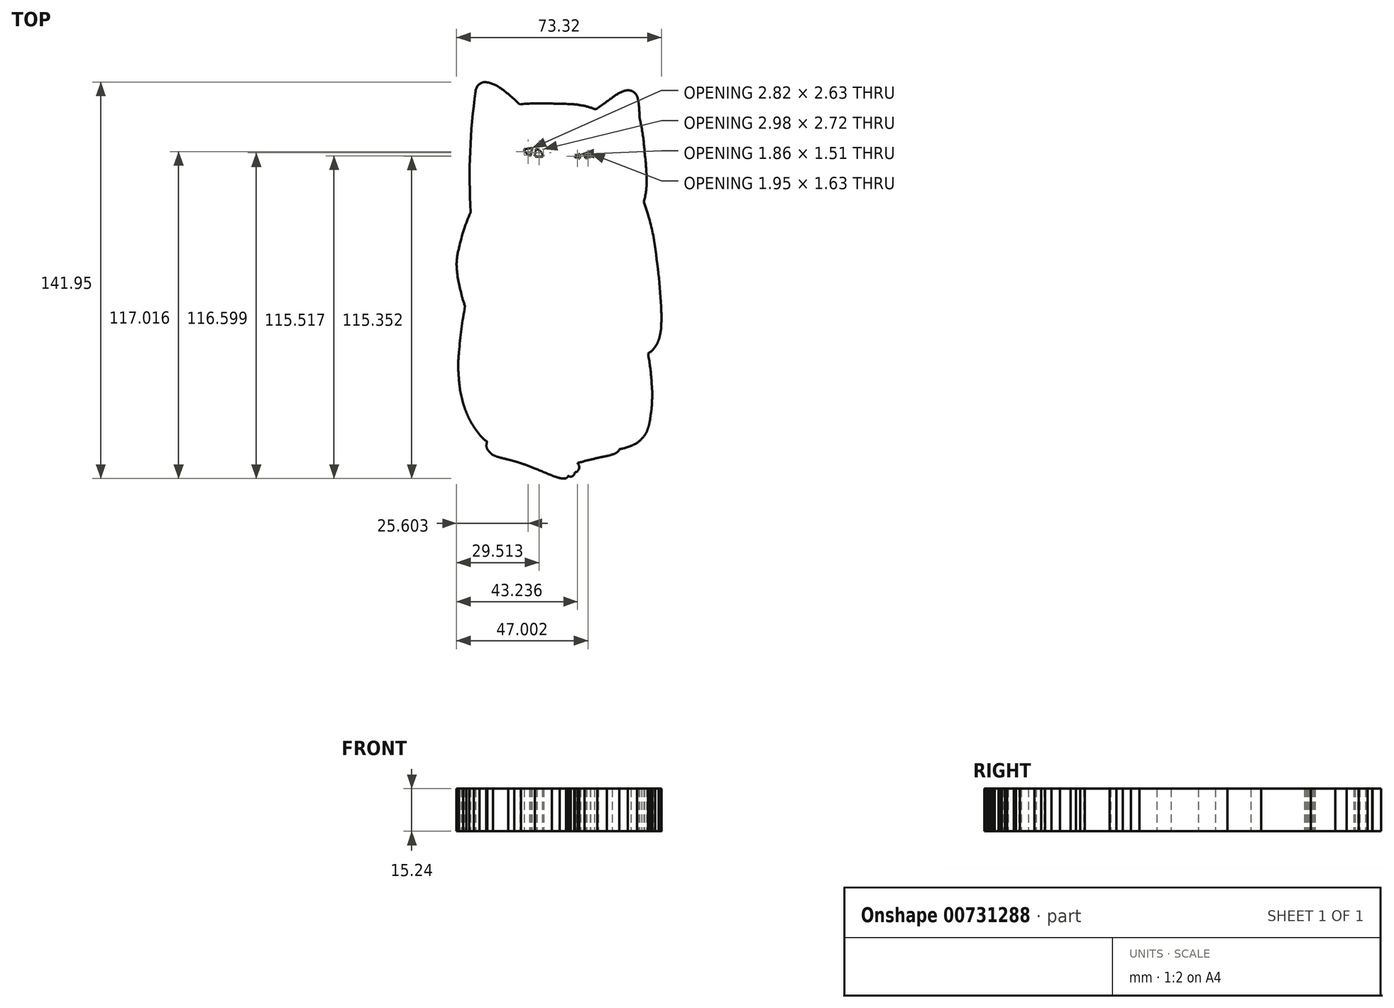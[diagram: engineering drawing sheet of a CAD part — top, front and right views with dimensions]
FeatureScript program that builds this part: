
annotation { "Feature Type Name" : "Feature", "Feature Type Description" : "" }
export const myFeature = defineFeature(function(context is Context, id is Id, definition is map)
    precondition{}
    {
        {
            var Q0;
            Q0=qCreatedBy(makeId("Top.planeOp"),FACE);
            var sketch = newSketch(context, id + "F0", { "sketchPlane" : qUnion([Q0])});
            skArc(sketch, "E0", {"start": v(-13.26, 64.15) * mm, "mid": v(-16.58, 67.18) * mm, "end": v(-20.13, 69.95) * mm});
            skArc(sketch, "E1", {"start": v(-20.13, 69.95) * mm, "mid": v(-22.73, 71.4) * mm, "end": v(-25.6, 72.18) * mm});
            skArc(sketch, "E2", {"start": v(-25.6, 72.18) * mm, "mid": v(-27.98, 71.2) * mm, "end": v(-29.08, 68.87) * mm});
            skArc(sketch, "E3", {"start": v(-29.08, 68.87) * mm, "mid": v(-31.04, 47.27) * mm, "end": v(-30.86, 25.58) * mm});
            skArc(sketch, "E4", {"start": v(-30.86, 25.58) * mm, "mid": v(-33.27, 19.33) * mm, "end": v(-35, 12.84) * mm});
            skArc(sketch, "E5", {"start": v(-35, 12.84) * mm, "mid": v(-35.66, 9.87) * mm, "end": v(-35.9, 6.83) * mm});
            skArc(sketch, "E6", {"start": v(-35.9, 6.83) * mm, "mid": v(-35.42, 1.9) * mm, "end": v(-34.32, -2.92) * mm});
            skArc(sketch, "E7", {"start": v(-34.32, -2.92) * mm, "mid": v(-33.74, -5.52) * mm, "end": v(-32.84, -8.04) * mm});
            skArc(sketch, "E8", {"start": v(-32.84, -8.04) * mm, "mid": v(-34.18, -16.26) * mm, "end": v(-35.03, -24.54) * mm});
            skArc(sketch, "E9", {"start": v(-35.03, -24.54) * mm, "mid": v(-35.3, -29.36) * mm, "end": v(-35.03, -34.17) * mm});
            skArc(sketch, "E10", {"start": v(-35.03, -34.17) * mm, "mid": v(-34.53, -38.6) * mm, "end": v(-33.48, -42.95) * mm});
            skArc(sketch, "E11", {"start": v(-33.48, -42.95) * mm, "mid": v(-33.01, -44.52) * mm, "end": v(-32.42, -46.04) * mm});
            skArc(sketch, "E12", {"start": v(-32.42, -46.04) * mm, "mid": v(-31.91, -47.22) * mm, "end": v(-31.4, -48.4) * mm});
            skArc(sketch, "E13", {"start": v(-31.4, -48.4) * mm, "mid": v(-30.6, -49.87) * mm, "end": v(-29.68, -51.27) * mm});
            skArc(sketch, "E14", {"start": v(-29.68, -51.27) * mm, "mid": v(-28.72, -52.66) * mm, "end": v(-27.72, -54.01) * mm});
            skArc(sketch, "E15", {"start": v(-27.72, -54.01) * mm, "mid": v(-26.47, -55.38) * mm, "end": v(-25.05, -56.58) * mm});
            skLineSegment(sketch, "E16", {"start": v(-24.94, -56.63) * mm, "end": v(-25.05, -56.58) * mm});
            skArc(sketch, "E17", {"start": v(-24.94, -56.63) * mm, "mid": v(-25.12, -57.06) * mm, "end": v(-25.2, -57.51) * mm});
            skArc(sketch, "E18", {"start": v(-25.2, -57.51) * mm, "mid": v(-25.2, -58.34) * mm, "end": v(-24.94, -59.13) * mm});
            skArc(sketch, "E19", {"start": v(-24.94, -59.13) * mm, "mid": v(-24.05, -60.33) * mm, "end": v(-22.9, -61.28) * mm});
            skArc(sketch, "E20", {"start": v(-22.9, -61.28) * mm, "mid": v(-21.83, -61.78) * mm, "end": v(-20.7, -62.14) * mm});
            skArc(sketch, "E21", {"start": v(-20.7, -62.14) * mm, "mid": v(-19.06, -62.56) * mm, "end": v(-17.43, -62.98) * mm});
            skArc(sketch, "E22", {"start": v(-15.23, -63.56) * mm, "mid": v(-16.33, -63.26) * mm, "end": v(-17.43, -62.98) * mm});
            skArc(sketch, "E23", {"start": v(-12.9, -64.3) * mm, "mid": v(-14.05, -63.9) * mm, "end": v(-15.23, -63.56) * mm});
            skArc(sketch, "E24", {"start": v(-7.9, -66.1) * mm, "mid": v(-10.38, -65.15) * mm, "end": v(-12.9, -64.3) * mm});
            skArc(sketch, "E25", {"start": v(-7.9, -66.1) * mm, "mid": v(-4.84, -67.4) * mm, "end": v(-1.78, -68.67) * mm});
            skArc(sketch, "E26", {"start": v(-1.78, -68.67) * mm, "mid": v(-0.43, -69.15) * mm, "end": v(0.95, -69.56) * mm});
            skArc(sketch, "E27", {"start": v(0.95, -69.56) * mm, "mid": v(2.1, -69.76) * mm, "end": v(3.24, -69.7) * mm});
            skArc(sketch, "E28", {"start": v(3.24, -69.7) * mm, "mid": v(3.75, -69.3) * mm, "end": v(4.13, -68.77) * mm});
            skArc(sketch, "E29", {"start": v(4.13, -68.77) * mm, "mid": v(4.48, -69.01) * mm, "end": v(4.9, -69.08) * mm});
            skArc(sketch, "E30", {"start": v(4.9, -69.08) * mm, "mid": v(5.7, -68.84) * mm, "end": v(6.24, -68.22) * mm});
            skArc(sketch, "E31", {"start": v(6.24, -68.22) * mm, "mid": v(6.4, -67.87) * mm, "end": v(6.5, -67.5) * mm});
            skArc(sketch, "E32", {"start": v(6.5, -67.5) * mm, "mid": v(7.09, -67.37) * mm, "end": v(7.53, -66.97) * mm});
            skArc(sketch, "E33", {"start": v(7.53, -66.97) * mm, "mid": v(7.79, -66.56) * mm, "end": v(7.96, -66.1) * mm});
            skArc(sketch, "E34", {"start": v(7.96, -66.1) * mm, "mid": v(7.96, -65.4) * mm, "end": v(7.72, -64.72) * mm});
            skArc(sketch, "E35", {"start": v(7.72, -64.72) * mm, "mid": v(7.62, -64.55) * mm, "end": v(7.46, -64.43) * mm});
            skLineSegment(sketch, "E36", {"start": v(7.46, -64.43) * mm, "end": v(7.46, -64.1) * mm});
            skArc(sketch, "E37", {"start": v(7.46, -64.1) * mm, "mid": v(8.7, -63.87) * mm, "end": v(9.9, -63.5) * mm});
            skArc(sketch, "E38", {"start": v(9.9, -63.5) * mm, "mid": v(12.18, -62.96) * mm, "end": v(14.45, -62.4) * mm});
            skArc(sketch, "E39", {"start": v(17.95, -61.7) * mm, "mid": v(16.2, -62.03) * mm, "end": v(14.45, -62.4) * mm});
            skArc(sketch, "E40", {"start": v(17.95, -61.7) * mm, "mid": v(19.35, -61.32) * mm, "end": v(20.72, -60.84) * mm});
            skArc(sketch, "E41", {"start": v(20.72, -60.84) * mm, "mid": v(21.72, -60.22) * mm, "end": v(22.4, -59.25) * mm});
            skArc(sketch, "E42", {"start": v(22.4, -59.25) * mm, "mid": v(23.94, -58.94) * mm, "end": v(25.44, -58.44) * mm});
            skArc(sketch, "E43", {"start": v(25.44, -58.44) * mm, "mid": v(27.08, -57.83) * mm, "end": v(28.65, -57.04) * mm});
            skArc(sketch, "E44", {"start": v(28.65, -57.04) * mm, "mid": v(30.19, -55.73) * mm, "end": v(31.48, -54.18) * mm});
            skArc(sketch, "E45", {"start": v(31.48, -54.18) * mm, "mid": v(32.14, -53.05) * mm, "end": v(32.57, -51.82) * mm});
            skArc(sketch, "E46", {"start": v(32.57, -51.82) * mm, "mid": v(32.96, -50.65) * mm, "end": v(33.23, -49.44) * mm});
            skArc(sketch, "E47", {"start": v(33.23, -49.44) * mm, "mid": v(33.35, -48.75) * mm, "end": v(33.42, -48.06) * mm});
            skArc(sketch, "E48", {"start": v(33.78, -45.75) * mm, "mid": v(33.6, -46.9) * mm, "end": v(33.42, -48.06) * mm});
            skArc(sketch, "E49", {"start": v(33.78, -45.75) * mm, "mid": v(33.95, -44.24) * mm, "end": v(34, -42.72) * mm});
            skArc(sketch, "E50", {"start": v(34, -42.72) * mm, "mid": v(34.12, -40.83) * mm, "end": v(34.12, -38.94) * mm});
            skArc(sketch, "E51", {"start": v(34.12, -38.94) * mm, "mid": v(34.08, -37.98) * mm, "end": v(34, -37.02) * mm});
            skArc(sketch, "E52", {"start": v(34, -37.02) * mm, "mid": v(33.96, -36.28) * mm, "end": v(33.89, -35.54) * mm});
            skArc(sketch, "E53", {"start": v(33.89, -35.54) * mm, "mid": v(33.87, -34.66) * mm, "end": v(33.79, -33.8) * mm});
            skArc(sketch, "E54", {"start": v(33.79, -33.8) * mm, "mid": v(33.32, -29.37) * mm, "end": v(32.6, -24.98) * mm});
            skArc(sketch, "E55", {"start": v(32.6, -24.98) * mm, "mid": v(34.05, -23.95) * mm, "end": v(35.17, -22.57) * mm});
            skArc(sketch, "E56", {"start": v(35.17, -22.57) * mm, "mid": v(35.9, -21.46) * mm, "end": v(36.4, -20.23) * mm});
            skArc(sketch, "E57", {"start": v(36.4, -20.23) * mm, "mid": v(36.83, -18.77) * mm, "end": v(37.13, -17.27) * mm});
            skArc(sketch, "E58", {"start": v(37.13, -17.27) * mm, "mid": v(37.34, -15.77) * mm, "end": v(37.37, -14.25) * mm});
            skArc(sketch, "E59", {"start": v(37.37, -14.25) * mm, "mid": v(37.43, -12.1) * mm, "end": v(37.37, -9.95) * mm});
            skArc(sketch, "E60", {"start": v(37.37, -9.95) * mm, "mid": v(36.33, 3.68) * mm, "end": v(34.49, 17.22) * mm});
            skArc(sketch, "E61", {"start": v(34.49, 17.22) * mm, "mid": v(33.01, 23.32) * mm, "end": v(31.1, 29.29) * mm});
            skArc(sketch, "E62", {"start": v(31.1, 29.29) * mm, "mid": v(31.89, 32.94) * mm, "end": v(32.15, 36.67) * mm});
            skArc(sketch, "E63", {"start": v(32.15, 36.67) * mm, "mid": v(31.93, 41.9) * mm, "end": v(31.37, 47.1) * mm});
            skArc(sketch, "E64", {"start": v(31.37, 47.1) * mm, "mid": v(30.99, 51.5) * mm, "end": v(30.34, 55.88) * mm});
            skArc(sketch, "E65", {"start": v(29.54, 59.85) * mm, "mid": v(29.9, 57.86) * mm, "end": v(30.34, 55.88) * mm});
            skArc(sketch, "E66", {"start": v(29.54, 59.85) * mm, "mid": v(29.5, 62.04) * mm, "end": v(29.3, 64.22) * mm});
            skArc(sketch, "E67", {"start": v(29.3, 64.22) * mm, "mid": v(29.06, 65.84) * mm, "end": v(28.54, 67.4) * mm});
            skArc(sketch, "E68", {"start": v(28.54, 67.4) * mm, "mid": v(27.73, 68.42) * mm, "end": v(26.58, 69.03) * mm});
            skArc(sketch, "E69", {"start": v(26.58, 69.03) * mm, "mid": v(25.43, 69.2) * mm, "end": v(24.28, 69.03) * mm});
            skArc(sketch, "E70", {"start": v(24.28, 69.03) * mm, "mid": v(21.94, 68.02) * mm, "end": v(19.85, 66.57) * mm});
            skArc(sketch, "E71", {"start": v(19.85, 66.57) * mm, "mid": v(17.33, 64.79) * mm, "end": v(14.82, 62.99) * mm});
            skArc(sketch, "E72", {"start": v(13.48, 62.46) * mm, "mid": v(14.2, 62.58) * mm, "end": v(14.82, 62.99) * mm});
            skArc(sketch, "E73", {"start": v(13.48, 62.46) * mm, "mid": v(11.03, 63.32) * mm, "end": v(8.5, 63.86) * mm});
            skArc(sketch, "E74", {"start": v(8.5, 63.86) * mm, "mid": v(6.85, 64.12) * mm, "end": v(5.19, 64.26) * mm});
            skArc(sketch, "E75", {"start": v(-4.66, 64.5) * mm, "mid": v(-8.96, 64.5) * mm, "end": v(-13.26, 64.15) * mm});
            skArc(sketch, "E76", {"start": v(5.19, 64.26) * mm, "mid": v(0.27, 64.42) * mm, "end": v(-4.66, 64.5) * mm});
            skArc(sketch, "E77", {"start": v(-25.6, 71.22) * mm, "mid": v(-27.28, 70.55) * mm, "end": v(-27.95, 68.87) * mm});
            skArc(sketch, "E78", {"start": v(-19.39, 68.5) * mm, "mid": v(-22.32, 70.26) * mm, "end": v(-25.6, 71.22) * mm});
            skArc(sketch, "E79", {"start": v(-15.35, 64.85) * mm, "mid": v(-17.26, 66.8) * mm, "end": v(-19.39, 68.5) * mm});
            skArc(sketch, "E80", {"start": v(-14.8, 64.3) * mm, "mid": v(-15.03, 64.62) * mm, "end": v(-15.35, 64.85) * mm});
            skArc(sketch, "E81", {"start": v(-15.09, 63.8) * mm, "mid": v(-14.84, 63.99) * mm, "end": v(-14.8, 64.3) * mm});
            skArc(sketch, "E82", {"start": v(-15.09, 63.8) * mm, "mid": v(-15.34, 63.67) * mm, "end": v(-15.46, 63.4) * mm});
            skArc(sketch, "E83", {"start": v(-15.46, 63.4) * mm, "mid": v(-15.36, 63.1) * mm, "end": v(-15.09, 62.91) * mm});
            skArc(sketch, "E84", {"start": v(-9.42, 63.55) * mm, "mid": v(-12.27, 63.36) * mm, "end": v(-15.09, 62.91) * mm});
            skArc(sketch, "E85", {"start": v(-0.75, 63.55) * mm, "mid": v(-5.09, 63.73) * mm, "end": v(-9.42, 63.55) * mm});
            skArc(sketch, "E86", {"start": v(8.17, 63.12) * mm, "mid": v(3.72, 63.52) * mm, "end": v(-0.75, 63.55) * mm});
            skArc(sketch, "E87", {"start": v(11.74, 62.2) * mm, "mid": v(9.97, 62.74) * mm, "end": v(8.17, 63.12) * mm});
            skArc(sketch, "E88", {"start": v(14.35, 61.15) * mm, "mid": v(13.08, 61.76) * mm, "end": v(11.74, 62.2) * mm});
            skArc(sketch, "E89", {"start": v(15.93, 59.97) * mm, "mid": v(15.2, 60.65) * mm, "end": v(14.35, 61.15) * mm});
            skArc(sketch, "E90", {"start": v(15.93, 59.97) * mm, "mid": v(16.46, 59.95) * mm, "end": v(16.61, 60.46) * mm});
            skArc(sketch, "E91", {"start": v(16.61, 60.46) * mm, "mid": v(16.16, 60.97) * mm, "end": v(15.63, 61.4) * mm});
            skArc(sketch, "E92", {"start": v(15.15, 61.93) * mm, "mid": v(15.32, 61.6) * mm, "end": v(15.63, 61.4) * mm});
            skLineSegment(sketch, "E93", {"start": v(18.79, 64.86) * mm, "end": v(15.22, 62.16) * mm});
            skArc(sketch, "E94", {"start": v(15.22, 62.16) * mm, "mid": v(15.15, 62.05) * mm, "end": v(15.15, 61.93) * mm});
            skArc(sketch, "E95", {"start": v(23.23, 67.61) * mm, "mid": v(20.95, 66.34) * mm, "end": v(18.79, 64.86) * mm});
            skArc(sketch, "E96", {"start": v(26.6, 68.34) * mm, "mid": v(24.85, 68.3) * mm, "end": v(23.23, 67.61) * mm});
            skArc(sketch, "E97", {"start": v(27.67, 67.31) * mm, "mid": v(27.23, 67.92) * mm, "end": v(26.6, 68.34) * mm});
            skArc(sketch, "E98", {"start": v(28.3, 65.47) * mm, "mid": v(28.07, 66.42) * mm, "end": v(27.67, 67.31) * mm});
            skArc(sketch, "E99", {"start": v(28.66, 62.26) * mm, "mid": v(28.56, 63.87) * mm, "end": v(28.3, 65.47) * mm});
            skArc(sketch, "E100", {"start": v(28.66, 62.26) * mm, "mid": v(28.76, 60.61) * mm, "end": v(28.92, 58.97) * mm});
            skArc(sketch, "E101", {"start": v(30, 52.86) * mm, "mid": v(29.82, 54.19) * mm, "end": v(29.62, 55.5) * mm});
            skArc(sketch, "E102", {"start": v(29.62, 55.5) * mm, "mid": v(29.33, 57.25) * mm, "end": v(28.92, 58.97) * mm});
            skArc(sketch, "E103", {"start": v(30.43, 49.6) * mm, "mid": v(30.25, 51.24) * mm, "end": v(30, 52.86) * mm});
            skArc(sketch, "E104", {"start": v(30.43, 49.6) * mm, "mid": v(30.54, 47.86) * mm, "end": v(30.68, 46.12) * mm});
            skArc(sketch, "E105", {"start": v(31, 43.26) * mm, "mid": v(30.86, 44.7) * mm, "end": v(30.68, 46.12) * mm});
            skArc(sketch, "E106", {"start": v(31.21, 40.83) * mm, "mid": v(31.12, 42.05) * mm, "end": v(31, 43.26) * mm});
            skArc(sketch, "E107", {"start": v(31.09, 34.8) * mm, "mid": v(31.16, 37.81) * mm, "end": v(31.21, 40.83) * mm});
            skArc(sketch, "E108", {"start": v(30.6, 31.77) * mm, "mid": v(30.92, 33.27) * mm, "end": v(31.09, 34.8) * mm});
            skArc(sketch, "E109", {"start": v(30.6, 31.77) * mm, "mid": v(30.27, 30.7) * mm, "end": v(29.95, 29.64) * mm});
            skArc(sketch, "E110", {"start": v(31.33, 26) * mm, "mid": v(30.69, 27.84) * mm, "end": v(29.95, 29.64) * mm});
            skArc(sketch, "E111", {"start": v(32.34, 22.74) * mm, "mid": v(31.86, 24.38) * mm, "end": v(31.33, 26) * mm});
            skArc(sketch, "E112", {"start": v(33.01, 19.96) * mm, "mid": v(32.72, 21.36) * mm, "end": v(32.34, 22.74) * mm});
            skArc(sketch, "E113", {"start": v(33.51, 17.52) * mm, "mid": v(33.28, 18.74) * mm, "end": v(33.01, 19.96) * mm});
            skArc(sketch, "E114", {"start": v(33.85, 15.67) * mm, "mid": v(33.71, 16.6) * mm, "end": v(33.51, 17.52) * mm});
            skArc(sketch, "E115", {"start": v(34.55, 11.43) * mm, "mid": v(34.24, 13.56) * mm, "end": v(33.85, 15.67) * mm});
            skArc(sketch, "E116", {"start": v(35.5, 4.62) * mm, "mid": v(35.09, 8.04) * mm, "end": v(34.55, 11.43) * mm});
            skArc(sketch, "E117", {"start": v(35.9, 0) * mm, "mid": v(35.76, 2.32) * mm, "end": v(35.5, 4.62) * mm});
            skArc(sketch, "E118", {"start": v(36.3, -5.46) * mm, "mid": v(36.16, -2.72) * mm, "end": v(35.9, 0) * mm});
            skArc(sketch, "E119", {"start": v(36.4, -9.9) * mm, "mid": v(36.4, -7.67) * mm, "end": v(36.3, -5.46) * mm});
            skArc(sketch, "E120", {"start": v(36.52, -13.76) * mm, "mid": v(36.47, -11.83) * mm, "end": v(36.4, -9.9) * mm});
            skArc(sketch, "E121", {"start": v(36.52, -15.6) * mm, "mid": v(36.54, -14.68) * mm, "end": v(36.52, -13.76) * mm});
            skArc(sketch, "E122", {"start": v(35.65, -19.72) * mm, "mid": v(36.23, -17.7) * mm, "end": v(36.52, -15.6) * mm});
            skArc(sketch, "E123", {"start": v(33.92, -22.57) * mm, "mid": v(34.9, -21.2) * mm, "end": v(35.65, -19.72) * mm});
            skArc(sketch, "E124", {"start": v(31.3, -24.18) * mm, "mid": v(32.74, -23.6) * mm, "end": v(33.92, -22.57) * mm});
            skArc(sketch, "E125", {"start": v(29.61, -23.69) * mm, "mid": v(30.41, -24.08) * mm, "end": v(31.3, -24.18) * mm});
            skArc(sketch, "E126", {"start": v(23.95, -19.4) * mm, "mid": v(26.58, -21.8) * mm, "end": v(29.61, -23.69) * mm});
            skArc(sketch, "E127", {"start": v(20.84, -15.32) * mm, "mid": v(22.33, -17.4) * mm, "end": v(23.95, -19.4) * mm});
            skArc(sketch, "E128", {"start": v(20.84, -15.32) * mm, "mid": v(19.8, -13.6) * mm, "end": v(18.76, -11.87) * mm});
            skArc(sketch, "E129", {"start": v(17.46, -8.91) * mm, "mid": v(18.07, -10.4) * mm, "end": v(18.76, -11.87) * mm});
            skArc(sketch, "E130", {"start": v(16.47, -5.65) * mm, "mid": v(16.93, -7.3) * mm, "end": v(17.46, -8.91) * mm});
            skArc(sketch, "E131", {"start": v(16.47, -5.65) * mm, "mid": v(16.21, -4.49) * mm, "end": v(15.72, -3.4) * mm});
            skArc(sketch, "E132", {"start": v(15.72, -3.4) * mm, "mid": v(15.11, -2.27) * mm, "end": v(14.33, -1.24) * mm});
            skArc(sketch, "E133", {"start": v(14.33, -1.24) * mm, "mid": v(13.47, -0.28) * mm, "end": v(12.45, 0.5) * mm});
            skArc(sketch, "E134", {"start": v(11.14, 3.5) * mm, "mid": v(11.66, 1.94) * mm, "end": v(12.45, 0.5) * mm});
            skArc(sketch, "E135", {"start": v(10.86, 5.84) * mm, "mid": v(10.83, 4.64) * mm, "end": v(11.14, 3.5) * mm});
            skArc(sketch, "E136", {"start": v(11.83, 6.04) * mm, "mid": v(11.32, 6.07) * mm, "end": v(10.86, 5.84) * mm});
            skArc(sketch, "E137", {"start": v(11.83, 6.04) * mm, "mid": v(12.23, 5.93) * mm, "end": v(12.63, 6.04) * mm});
            skArc(sketch, "E138", {"start": v(12.63, 6.04) * mm, "mid": v(12.8, 6.3) * mm, "end": v(12.8, 6.62) * mm});
            skArc(sketch, "E139", {"start": v(13.3, 7.62) * mm, "mid": v(12.9, 7.2) * mm, "end": v(12.8, 6.62) * mm});
            skArc(sketch, "E140", {"start": v(13.81, 7.62) * mm, "mid": v(13.56, 7.71) * mm, "end": v(13.3, 7.62) * mm});
            skArc(sketch, "E141", {"start": v(14.18, 7.16) * mm, "mid": v(14.03, 7.41) * mm, "end": v(13.81, 7.62) * mm});
            skArc(sketch, "E142", {"start": v(14.18, 7.16) * mm, "mid": v(14.47, 7.1) * mm, "end": v(14.75, 7.16) * mm});
            skArc(sketch, "E143", {"start": v(14.75, 7.16) * mm, "mid": v(14.87, 7.35) * mm, "end": v(14.92, 7.56) * mm});
            skArc(sketch, "E144", {"start": v(14.92, 7.56) * mm, "mid": v(14.74, 8.04) * mm, "end": v(14.5, 8.5) * mm});
            skArc(sketch, "E145", {"start": v(13.52, 11.92) * mm, "mid": v(13.94, 10.19) * mm, "end": v(14.5, 8.5) * mm});
            skArc(sketch, "E146", {"start": v(13.17, 14.34) * mm, "mid": v(13.3, 13.12) * mm, "end": v(13.52, 11.92) * mm});
            skArc(sketch, "E147", {"start": v(14.59, 14.59) * mm, "mid": v(13.81, 14.87) * mm, "end": v(13.17, 14.34) * mm});
            skArc(sketch, "E148", {"start": v(16.72, 9.6) * mm, "mid": v(15.7, 12.11) * mm, "end": v(14.59, 14.59) * mm});
            skArc(sketch, "E149", {"start": v(16.72, 9.22) * mm, "mid": v(16.72, 9.4) * mm, "end": v(16.72, 9.6) * mm});
            skArc(sketch, "E150", {"start": v(16.72, 9.22) * mm, "mid": v(16.97, 9) * mm, "end": v(17.31, 8.93) * mm});
            skArc(sketch, "E151", {"start": v(19.27, 9.22) * mm, "mid": v(18.26, 9.3) * mm, "end": v(17.31, 8.93) * mm});
            skArc(sketch, "E152", {"start": v(20.5, 7.32) * mm, "mid": v(20.1, 8.41) * mm, "end": v(19.27, 9.22) * mm});
            skArc(sketch, "E153", {"start": v(20.5, 6.44) * mm, "mid": v(20.51, 6.88) * mm, "end": v(20.5, 7.32) * mm});
            skArc(sketch, "E154", {"start": v(20.5, 6.44) * mm, "mid": v(20.96, 6.2) * mm, "end": v(21.42, 6.44) * mm});
            skArc(sketch, "E155", {"start": v(21.42, 6.44) * mm, "mid": v(21.45, 6.91) * mm, "end": v(21.45, 7.39) * mm});
            skArc(sketch, "E156", {"start": v(21.93, 7.7) * mm, "mid": v(21.62, 7.65) * mm, "end": v(21.45, 7.39) * mm});
            skArc(sketch, "E157", {"start": v(23.1, 7.26) * mm, "mid": v(22.57, 7.65) * mm, "end": v(21.93, 7.7) * mm});
            skArc(sketch, "E158", {"start": v(24.39, 4.96) * mm, "mid": v(23.97, 6.24) * mm, "end": v(23.1, 7.26) * mm});
            skArc(sketch, "E159", {"start": v(24.59, 2.74) * mm, "mid": v(24.56, 3.86) * mm, "end": v(24.39, 4.96) * mm});
            skArc(sketch, "E160", {"start": v(24.39, 1.17) * mm, "mid": v(24.57, 1.95) * mm, "end": v(24.59, 2.74) * mm});
            skArc(sketch, "E161", {"start": v(24.39, 1.17) * mm, "mid": v(24.3, 0.85) * mm, "end": v(24.39, 0.53) * mm});
            skArc(sketch, "E162", {"start": v(24.39, 0.53) * mm, "mid": v(24.75, 0.37) * mm, "end": v(25.14, 0.32) * mm});
            skArc(sketch, "E163", {"start": v(25.14, 0.32) * mm, "mid": v(26.14, -1.9) * mm, "end": v(27.2, -4.1) * mm});
            skArc(sketch, "E164", {"start": v(27.2, -4.1) * mm, "mid": v(28.44, -6.92) * mm, "end": v(29.73, -9.72) * mm});
            skArc(sketch, "E165", {"start": v(29.73, -9.72) * mm, "mid": v(29.67, -10.08) * mm, "end": v(29.73, -10.44) * mm});
            skArc(sketch, "E166", {"start": v(29.73, -10.44) * mm, "mid": v(30.22, -10.95) * mm, "end": v(30.85, -10.63) * mm});
            skArc(sketch, "E167", {"start": v(30.85, -10.63) * mm, "mid": v(30.75, -10.05) * mm, "end": v(30.58, -9.5) * mm});
            skArc(sketch, "E168", {"start": v(30.58, -9.5) * mm, "mid": v(28.14, -4.01) * mm, "end": v(25.63, 1.44) * mm});
            skArc(sketch, "E169", {"start": v(25.51, 1.99) * mm, "mid": v(25.53, 1.7) * mm, "end": v(25.63, 1.44) * mm});
            skArc(sketch, "E170", {"start": v(25.51, 1.99) * mm, "mid": v(25.61, 3.02) * mm, "end": v(25.51, 4.06) * mm});
            skArc(sketch, "E171", {"start": v(25.51, 4.06) * mm, "mid": v(25.26, 5.36) * mm, "end": v(24.7, 6.56) * mm});
            skArc(sketch, "E172", {"start": v(24.7, 6.56) * mm, "mid": v(24.16, 7.47) * mm, "end": v(23.36, 8.17) * mm});
            skArc(sketch, "E173", {"start": v(23.36, 8.17) * mm, "mid": v(22.61, 8.5) * mm, "end": v(21.8, 8.57) * mm});
            skLineSegment(sketch, "E174", {"start": v(21.8, 8.57) * mm, "end": v(21.01, 8.57) * mm});
            skArc(sketch, "E175", {"start": v(21.01, 8.57) * mm, "mid": v(20.34, 9.46) * mm, "end": v(19.39, 10.04) * mm});
            skArc(sketch, "E176", {"start": v(19.39, 10.04) * mm, "mid": v(18.64, 10.24) * mm, "end": v(17.86, 10.16) * mm});
            skArc(sketch, "E177", {"start": v(13.32, 15.8) * mm, "mid": v(12.57, 15.28) * mm, "end": v(12.2, 14.46) * mm});
            skArc(sketch, "E178", {"start": v(15.21, 15.52) * mm, "mid": v(14.3, 15.87) * mm, "end": v(13.32, 15.8) * mm});
            skLineSegment(sketch, "E179", {"start": v(17.86, 10.16) * mm, "end": v(15.57, 15.13) * mm});
            skArc(sketch, "E180", {"start": v(15.57, 15.13) * mm, "mid": v(15.42, 15.35) * mm, "end": v(15.21, 15.52) * mm});
            skArc(sketch, "E181", {"start": v(12.2, 14.46) * mm, "mid": v(12.11, 12.95) * mm, "end": v(12.26, 11.44) * mm});
            skArc(sketch, "E182", {"start": v(12.26, 11.44) * mm, "mid": v(12.62, 10.2) * mm, "end": v(13.07, 9) * mm});
            skArc(sketch, "E183", {"start": v(13.1, 8.57) * mm, "mid": v(12.27, 8) * mm, "end": v(11.84, 7.09) * mm});
            skArc(sketch, "E184", {"start": v(13.07, 9) * mm, "mid": v(13.03, 8.78) * mm, "end": v(13.1, 8.57) * mm});
            skArc(sketch, "E185", {"start": v(11.84, 7.09) * mm, "mid": v(10.98, 6.97) * mm, "end": v(10.21, 6.57) * mm});
            skArc(sketch, "E186", {"start": v(10.21, 6.57) * mm, "mid": v(9.96, 6.27) * mm, "end": v(9.85, 5.9) * mm});
            skLineSegment(sketch, "E187", {"start": v(9.85, 5.9) * mm, "end": v(9.97, 4) * mm});
            skArc(sketch, "E188", {"start": v(9.97, 4) * mm, "mid": v(10.2, 2.9) * mm, "end": v(10.7, 1.88) * mm});
            skArc(sketch, "E189", {"start": v(10.7, 1.88) * mm, "mid": v(11.18, 0.77) * mm, "end": v(11.83, -0.24) * mm});
            skArc(sketch, "E190", {"start": v(14.11, -2.52) * mm, "mid": v(13.07, -1.28) * mm, "end": v(11.83, -0.24) * mm});
            skArc(sketch, "E191", {"start": v(15.6, -5.93) * mm, "mid": v(15, -4.16) * mm, "end": v(14.11, -2.52) * mm});
            skArc(sketch, "E192", {"start": v(15.6, -5.93) * mm, "mid": v(16.17, -8) * mm, "end": v(16.93, -10.02) * mm});
            skArc(sketch, "E193", {"start": v(16.93, -10.02) * mm, "mid": v(18.02, -12.48) * mm, "end": v(19.39, -14.8) * mm});
            skArc(sketch, "E194", {"start": v(19.39, -14.8) * mm, "mid": v(20.35, -16.3) * mm, "end": v(21.39, -17.75) * mm});
            skArc(sketch, "E195", {"start": v(21.39, -18.22) * mm, "mid": v(21.46, -17.99) * mm, "end": v(21.39, -17.75) * mm});
            skArc(sketch, "E196", {"start": v(21.39, -18.22) * mm, "mid": v(19.32, -19.49) * mm, "end": v(17.33, -20.86) * mm});
            skArc(sketch, "E197", {"start": v(17.33, -20.86) * mm, "mid": v(15.52, -22.34) * mm, "end": v(13.8, -23.93) * mm});
            skArc(sketch, "E198", {"start": v(13.8, -23.93) * mm, "mid": v(12.38, -25.5) * mm, "end": v(11.2, -27.24) * mm});
            skArc(sketch, "E199", {"start": v(11.2, -27.24) * mm, "mid": v(9.93, -29.07) * mm, "end": v(8.91, -31.05) * mm});
            skArc(sketch, "E200", {"start": v(8.91, -31.05) * mm, "mid": v(8.05, -33.31) * mm, "end": v(7.37, -35.63) * mm});
            skArc(sketch, "E201", {"start": v(7.37, -35.63) * mm, "mid": v(6.98, -37.3) * mm, "end": v(6.67, -39) * mm});
            skArc(sketch, "E202", {"start": v(6.67, -39) * mm, "mid": v(6.4, -40.95) * mm, "end": v(6.32, -42.9) * mm});
            skArc(sketch, "E203", {"start": v(6.32, -42.9) * mm, "mid": v(6.3, -45.53) * mm, "end": v(6.48, -48.15) * mm});
            skArc(sketch, "E204", {"start": v(6.48, -48.15) * mm, "mid": v(6.68, -49.3) * mm, "end": v(6.93, -50.44) * mm});
            skArc(sketch, "E205", {"start": v(4.18, -54.12) * mm, "mid": v(5.81, -52.47) * mm, "end": v(6.93, -50.44) * mm});
            skArc(sketch, "E206", {"start": v(0.3, -56.09) * mm, "mid": v(2.32, -55.27) * mm, "end": v(4.18, -54.12) * mm});
            skArc(sketch, "E207", {"start": v(0.3, -56.09) * mm, "mid": v(-1.57, -54.66) * mm, "end": v(-3.7, -53.66) * mm});
            skArc(sketch, "E208", {"start": v(-3.7, -52.8) * mm, "mid": v(-3.89, -53.23) * mm, "end": v(-3.7, -53.66) * mm});
            skArc(sketch, "E209", {"start": v(-3.7, -52.8) * mm, "mid": v(-2.77, -50.8) * mm, "end": v(-2.23, -48.65) * mm});
            skArc(sketch, "E210", {"start": v(-2.23, -48.65) * mm, "mid": v(-1.91, -46.73) * mm, "end": v(-1.75, -44.8) * mm});
            skArc(sketch, "E211", {"start": v(-1.75, -44.8) * mm, "mid": v(-1.77, -42.6) * mm, "end": v(-1.9, -40.4) * mm});
            skArc(sketch, "E212", {"start": v(-1.9, -40.4) * mm, "mid": v(-2.15, -37.33) * mm, "end": v(-2.66, -34.3) * mm});
            skArc(sketch, "E213", {"start": v(-2.66, -34.3) * mm, "mid": v(-3.2, -31.64) * mm, "end": v(-4, -29.06) * mm});
            skArc(sketch, "E214", {"start": v(-4, -29.06) * mm, "mid": v(-4.64, -27.5) * mm, "end": v(-5.45, -26.03) * mm});
            skArc(sketch, "E215", {"start": v(-5.45, -26.03) * mm, "mid": v(-6.5, -24.17) * mm, "end": v(-7.84, -22.5) * mm});
            skArc(sketch, "E216", {"start": v(-7.84, -22.5) * mm, "mid": v(-9.84, -20.4) * mm, "end": v(-12.09, -18.55) * mm});
            skArc(sketch, "E217", {"start": v(-12.09, -18.55) * mm, "mid": v(-12.6, -18.67) * mm, "end": v(-12.67, -19.19) * mm});
            skArc(sketch, "E218", {"start": v(-8.73, -22.95) * mm, "mid": v(-10.6, -20.97) * mm, "end": v(-12.67, -19.19) * mm});
            skArc(sketch, "E219", {"start": v(-5.45, -28.18) * mm, "mid": v(-6.91, -25.45) * mm, "end": v(-8.73, -22.95) * mm});
            skArc(sketch, "E220", {"start": v(-3.9, -33.2) * mm, "mid": v(-4.5, -30.64) * mm, "end": v(-5.45, -28.18) * mm});
            skArc(sketch, "E221", {"start": v(-3.05, -38.39) * mm, "mid": v(-3.37, -35.78) * mm, "end": v(-3.9, -33.2) * mm});
            skArc(sketch, "E222", {"start": v(-2.66, -43.23) * mm, "mid": v(-2.77, -40.8) * mm, "end": v(-3.05, -38.39) * mm});
            skArc(sketch, "E223", {"start": v(-3.05, -47.5) * mm, "mid": v(-2.75, -45.37) * mm, "end": v(-2.66, -43.23) * mm});
            skArc(sketch, "E224", {"start": v(-4.18, -51.53) * mm, "mid": v(-3.48, -49.55) * mm, "end": v(-3.05, -47.5) * mm});
            skArc(sketch, "E225", {"start": v(-4.18, -51.53) * mm, "mid": v(-4.6, -52.4) * mm, "end": v(-5.03, -53.26) * mm});
            skArc(sketch, "E226", {"start": v(-5.03, -53.26) * mm, "mid": v(-5.67, -53.22) * mm, "end": v(-6.3, -53.26) * mm});
            skArc(sketch, "E227", {"start": v(-6.3, -53.26) * mm, "mid": v(-6.6, -53.74) * mm, "end": v(-6.3, -54.21) * mm});
            skArc(sketch, "E228", {"start": v(-2.9, -54.99) * mm, "mid": v(-4.54, -54.34) * mm, "end": v(-6.3, -54.21) * mm});
            skArc(sketch, "E229", {"start": v(-1.2, -56.28) * mm, "mid": v(-2, -55.57) * mm, "end": v(-2.9, -54.99) * mm});
            skArc(sketch, "E230", {"start": v(-1.54, -56.83) * mm, "mid": v(-1.2, -56.66) * mm, "end": v(-1.2, -56.28) * mm});
            skArc(sketch, "E231", {"start": v(-1.54, -56.83) * mm, "mid": v(-3.37, -57.6) * mm, "end": v(-4.87, -58.9) * mm});
            skArc(sketch, "E232", {"start": v(-4.87, -58.9) * mm, "mid": v(-5.4, -60.37) * mm, "end": v(-5, -61.89) * mm});
            skArc(sketch, "E233", {"start": v(-5, -62.18) * mm, "mid": v(-4.98, -62.03) * mm, "end": v(-5, -61.89) * mm});
            skArc(sketch, "E234", {"start": v(-5, -62.18) * mm, "mid": v(-5.18, -63.17) * mm, "end": v(-4.8, -64.1) * mm});
            skArc(sketch, "E235", {"start": v(-4.8, -64.1) * mm, "mid": v(-4.41, -64.53) * mm, "end": v(-3.89, -64.78) * mm});
            skArc(sketch, "E236", {"start": v(-3.78, -64.78) * mm, "mid": v(-3.78, -65.35) * mm, "end": v(-3.62, -65.9) * mm});
            skArc(sketch, "E237", {"start": v(-4.2, -66.53) * mm, "mid": v(-3.7, -66.4) * mm, "end": v(-3.62, -65.9) * mm});
            skArc(sketch, "E238", {"start": v(-4.2, -66.53) * mm, "mid": v(-8.3, -64.86) * mm, "end": v(-12.48, -63.47) * mm});
            skArc(sketch, "E239", {"start": v(-12.48, -63.47) * mm, "mid": v(-16.43, -62.26) * mm, "end": v(-20.43, -61.23) * mm});
            skArc(sketch, "E240", {"start": v(-24, -58.6) * mm, "mid": v(-22.49, -60.27) * mm, "end": v(-20.43, -61.23) * mm});
            skArc(sketch, "E241", {"start": v(-24, -56.95) * mm, "mid": v(-24.14, -57.77) * mm, "end": v(-24, -58.6) * mm});
            skArc(sketch, "E242", {"start": v(-24, -56.95) * mm, "mid": v(-23.81, -56.6) * mm, "end": v(-24, -56.23) * mm});
            skArc(sketch, "E243", {"start": v(-26.8, -53.5) * mm, "mid": v(-25.43, -54.9) * mm, "end": v(-24, -56.23) * mm});
            skArc(sketch, "E244", {"start": v(-29.76, -49.09) * mm, "mid": v(-28.4, -51.37) * mm, "end": v(-26.8, -53.5) * mm});
            skArc(sketch, "E245", {"start": v(-32.34, -42.93) * mm, "mid": v(-31.2, -46.07) * mm, "end": v(-29.76, -49.09) * mm});
            skArc(sketch, "E246", {"start": v(-33.83, -35.08) * mm, "mid": v(-33.33, -39.05) * mm, "end": v(-32.34, -42.93) * mm});
            skArc(sketch, "E247", {"start": v(-33.83, -23.32) * mm, "mid": v(-34.13, -29.2) * mm, "end": v(-33.83, -35.08) * mm});
            skArc(sketch, "E248", {"start": v(-32.34, -12.18) * mm, "mid": v(-33.13, -17.74) * mm, "end": v(-33.83, -23.32) * mm});
            skArc(sketch, "E249", {"start": v(-31.43, -12.18) * mm, "mid": v(-31.88, -11.8) * mm, "end": v(-32.34, -12.18) * mm});
            skArc(sketch, "E250", {"start": v(-31.43, -12.18) * mm, "mid": v(-30.2, -14.67) * mm, "end": v(-28.12, -16.49) * mm});
            skArc(sketch, "E251", {"start": v(-28.12, -16.49) * mm, "mid": v(-25.05, -17.48) * mm, "end": v(-21.99, -16.49) * mm});
            skArc(sketch, "E252", {"start": v(-21.99, -16.49) * mm, "mid": v(-17.6, -13.1) * mm, "end": v(-13.5, -9.4) * mm});
            skArc(sketch, "E253", {"start": v(-13.5, -9.4) * mm, "mid": v(-7.8, -4.36) * mm, "end": v(-2.36, 0.95) * mm});
            skArc(sketch, "E254", {"start": v(-2.36, 0.95) * mm, "mid": v(2.42, 3.97) * mm, "end": v(4.6, 9.19) * mm});
            skArc(sketch, "E255", {"start": v(4.6, 9.19) * mm, "mid": v(4.08, 10.41) * mm, "end": v(2.91, 11.05) * mm});
            skArc(sketch, "E256", {"start": v(2.91, 11.05) * mm, "mid": v(2.26, 11.98) * mm, "end": v(1.33, 12.63) * mm});
            skArc(sketch, "E257", {"start": v(1.33, 13.27) * mm, "mid": v(1.2, 12.95) * mm, "end": v(1.33, 12.63) * mm});
            skLineSegment(sketch, "E258", {"start": v(1.33, 13.27) * mm, "end": v(2.66, 16.12) * mm});
            skArc(sketch, "E259", {"start": v(2.66, 16.05) * mm, "mid": v(2.35, 17.28) * mm, "end": v(1.4, 18.12) * mm});
            skArc(sketch, "E260", {"start": v(1.4, 18.12) * mm, "mid": v(0.45, 18.3) * mm, "end": v(-0.45, 17.95) * mm});
            skArc(sketch, "E261", {"start": v(-0.45, 17.95) * mm, "mid": v(-1.1, 17.52) * mm, "end": v(-1.65, 16.98) * mm});
            skArc(sketch, "E262", {"start": v(-1.65, 16.98) * mm, "mid": v(-2.68, 15.71) * mm, "end": v(-3.52, 14.31) * mm});
            skArc(sketch, "E263", {"start": v(-3.52, 14.31) * mm, "mid": v(-4.4, 14.35) * mm, "end": v(-5.28, 14.2) * mm});
            skArc(sketch, "E264", {"start": v(-5.28, 14.2) * mm, "mid": v(-6, 13.71) * mm, "end": v(-6.5, 13) * mm});
            skArc(sketch, "E265", {"start": v(-7.09, 13) * mm, "mid": v(-6.8, 12.9) * mm, "end": v(-6.5, 13) * mm});
            skArc(sketch, "E266", {"start": v(-7.09, 13) * mm, "mid": v(-8.06, 13.23) * mm, "end": v(-9.04, 13) * mm});
            skArc(sketch, "E267", {"start": v(-9.04, 13) * mm, "mid": v(-9.86, 12.64) * mm, "end": v(-10.5, 12) * mm});
            skArc(sketch, "E268", {"start": v(-10.5, 12) * mm, "mid": v(-11.03, 11.15) * mm, "end": v(-11.38, 10.22) * mm});
            skArc(sketch, "E269", {"start": v(-11.38, 10.22) * mm, "mid": v(-11.55, 9.4) * mm, "end": v(-11.6, 8.57) * mm});
            skArc(sketch, "E270", {"start": v(-11.6, 8.57) * mm, "mid": v(-13.23, 7.8) * mm, "end": v(-14.85, 7.03) * mm});
            skLineSegment(sketch, "E271", {"start": v(-14.85, 7.03) * mm, "end": v(-19.04, 4.8) * mm});
            skArc(sketch, "E272", {"start": v(-19.8, 4.95) * mm, "mid": v(-19.45, 4.74) * mm, "end": v(-19.04, 4.8) * mm});
            skArc(sketch, "E273", {"start": v(-19.35, 8.32) * mm, "mid": v(-19.77, 6.66) * mm, "end": v(-19.8, 4.95) * mm});
            skArc(sketch, "E274", {"start": v(-19.35, 8.32) * mm, "mid": v(-19.28, 8.85) * mm, "end": v(-19.63, 9.26) * mm});
            skArc(sketch, "E275", {"start": v(-19.63, 9.26) * mm, "mid": v(-20.06, 9.1) * mm, "end": v(-20.2, 8.67) * mm});
            skArc(sketch, "E276", {"start": v(-20.2, 8.67) * mm, "mid": v(-20.58, 7.39) * mm, "end": v(-20.79, 6.06) * mm});
            skArc(sketch, "E277", {"start": v(-20.79, 6.06) * mm, "mid": v(-20.89, 4.87) * mm, "end": v(-20.9, 3.68) * mm});
            skArc(sketch, "E278", {"start": v(-20.9, 3.68) * mm, "mid": v(-22.36, 2.9) * mm, "end": v(-23.76, 2) * mm});
            skArc(sketch, "E279", {"start": v(-26.27, 0.2) * mm, "mid": v(-25.01, 1.1) * mm, "end": v(-23.76, 2) * mm});
            skArc(sketch, "E280", {"start": v(-26.27, 0.2) * mm, "mid": v(-26.97, -0.38) * mm, "end": v(-27.64, -0.99) * mm});
            skArc(sketch, "E281", {"start": v(-27.64, -0.99) * mm, "mid": v(-27.67, -1.33) * mm, "end": v(-27.4, -1.56) * mm});
            skArc(sketch, "E282", {"start": v(-27.4, -1.56) * mm, "mid": v(-26.86, -1.66) * mm, "end": v(-26.49, -1.25) * mm});
            skArc(sketch, "E283", {"start": v(-19.14, 3.68) * mm, "mid": v(-22.89, 1.33) * mm, "end": v(-26.49, -1.25) * mm});
            skArc(sketch, "E284", {"start": v(-11.6, 7.46) * mm, "mid": v(-15.43, 5.7) * mm, "end": v(-19.14, 3.68) * mm});
            skArc(sketch, "E285", {"start": v(-11.1, 7.25) * mm, "mid": v(-11.32, 7.43) * mm, "end": v(-11.6, 7.46) * mm});
            skArc(sketch, "E286", {"start": v(-10.28, 10.21) * mm, "mid": v(-10.61, 8.85) * mm, "end": v(-10.66, 7.46) * mm});
            skArc(sketch, "E287", {"start": v(-11.1, 7.25) * mm, "mid": v(-10.83, 7.26) * mm, "end": v(-10.66, 7.46) * mm});
            skArc(sketch, "E288", {"start": v(-8.95, 12) * mm, "mid": v(-9.83, 11.26) * mm, "end": v(-10.28, 10.21) * mm});
            skArc(sketch, "E289", {"start": v(-7.14, 12) * mm, "mid": v(-8.05, 12.13) * mm, "end": v(-8.95, 12) * mm});
            skArc(sketch, "E290", {"start": v(-7.02, 11.06) * mm, "mid": v(-7.06, 11.54) * mm, "end": v(-7.14, 12) * mm});
            skArc(sketch, "E291", {"start": v(-7, 11.06) * mm, "mid": v(-6.48, 10.73) * mm, "end": v(-6.01, 11.13) * mm});
            skArc(sketch, "E292", {"start": v(-5.31, 13.03) * mm, "mid": v(-5.84, 12.15) * mm, "end": v(-6.01, 11.13) * mm});
            skArc(sketch, "E293", {"start": v(-3.9, 13.34) * mm, "mid": v(-4.65, 13.39) * mm, "end": v(-5.31, 13.03) * mm});
            skArc(sketch, "E294", {"start": v(-3.9, 13.34) * mm, "mid": v(-3.68, 13) * mm, "end": v(-3.28, 12.87) * mm});
            skArc(sketch, "E295", {"start": v(-3.28, 12.87) * mm, "mid": v(-2.9, 13) * mm, "end": v(-2.7, 13.34) * mm});
            skArc(sketch, "E296", {"start": v(-0.54, 16.3) * mm, "mid": v(-1.73, 14.9) * mm, "end": v(-2.7, 13.34) * mm});
            skArc(sketch, "E297", {"start": v(0.54, 17.16) * mm, "mid": v(-0.05, 16.78) * mm, "end": v(-0.54, 16.3) * mm});
            skArc(sketch, "E298", {"start": v(1.55, 16.48) * mm, "mid": v(1.23, 17.1) * mm, "end": v(0.54, 17.16) * mm});
            skArc(sketch, "E299", {"start": v(0.87, 15.05) * mm, "mid": v(1.3, 15.72) * mm, "end": v(1.55, 16.48) * mm});
            skArc(sketch, "E300", {"start": v(0.87, 15.05) * mm, "mid": v(0.02, 13.68) * mm, "end": v(-0.82, 12.3) * mm});
            skArc(sketch, "E301", {"start": v(-0.82, 12.3) * mm, "mid": v(-0.92, 11.64) * mm, "end": v(-0.33, 11.32) * mm});
            skArc(sketch, "E302", {"start": v(1.37, 11.36) * mm, "mid": v(0.52, 11.46) * mm, "end": v(-0.33, 11.32) * mm});
            skArc(sketch, "E303", {"start": v(1.37, 10.52) * mm, "mid": v(1.69, 10.94) * mm, "end": v(1.37, 11.36) * mm});
            skArc(sketch, "E304", {"start": v(1.37, 10.52) * mm, "mid": v(1.1, 10.04) * mm, "end": v(1.37, 9.55) * mm});
            skArc(sketch, "E305", {"start": v(1.37, 9.55) * mm, "mid": v(1.97, 9.6) * mm, "end": v(2.4, 10.04) * mm});
            skArc(sketch, "E306", {"start": v(3.4, 9.55) * mm, "mid": v(3.03, 10.06) * mm, "end": v(2.4, 10.04) * mm});
            skArc(sketch, "E307", {"start": v(2.91, 6.8) * mm, "mid": v(3.41, 8.13) * mm, "end": v(3.4, 9.55) * mm});
            skArc(sketch, "E308", {"start": v(0.8, 3.66) * mm, "mid": v(2, 5.14) * mm, "end": v(2.91, 6.8) * mm});
            skArc(sketch, "E309", {"start": v(-2.79, 2) * mm, "mid": v(-0.84, 2.49) * mm, "end": v(0.8, 3.66) * mm});
            skArc(sketch, "E310", {"start": v(-13.86, -8.35) * mm, "mid": v(-8.29, -3.22) * mm, "end": v(-2.79, 2) * mm});
            skArc(sketch, "E311", {"start": v(-20.6, -14.24) * mm, "mid": v(-17.2, -11.33) * mm, "end": v(-13.86, -8.35) * mm});
            skArc(sketch, "E312", {"start": v(-25.46, -16.43) * mm, "mid": v(-22.86, -15.71) * mm, "end": v(-20.6, -14.24) * mm});
            skArc(sketch, "E313", {"start": v(-30.44, -11.69) * mm, "mid": v(-28.62, -14.76) * mm, "end": v(-25.46, -16.43) * mm});
            skArc(sketch, "E314", {"start": v(-31.11, -7.8) * mm, "mid": v(-30.9, -9.76) * mm, "end": v(-30.44, -11.69) * mm});
            skArc(sketch, "E315", {"start": v(-33.8, -0.56) * mm, "mid": v(-32.72, -4.27) * mm, "end": v(-31.11, -7.8) * mm});
            skArc(sketch, "E316", {"start": v(-34.48, 9.25) * mm, "mid": v(-34.6, 4.31) * mm, "end": v(-33.8, -0.56) * mm});
            skArc(sketch, "E317", {"start": v(-33.28, 15.14) * mm, "mid": v(-34.03, 12.22) * mm, "end": v(-34.48, 9.25) * mm});
            skArc(sketch, "E318", {"start": v(-30.44, 24.24) * mm, "mid": v(-31.96, 19.72) * mm, "end": v(-33.28, 15.14) * mm});
            skArc(sketch, "E319", {"start": v(-30.44, 24.24) * mm, "mid": v(-30.1, 24.82) * mm, "end": v(-29.82, 25.41) * mm});
            skArc(sketch, "E320", {"start": v(-30.15, 43.54) * mm, "mid": v(-30.3, 34.47) * mm, "end": v(-29.82, 25.41) * mm});
            skArc(sketch, "E321", {"start": v(-30.15, 43.54) * mm, "mid": v(-29.8, 48.7) * mm, "end": v(-29.56, 53.88) * mm});
            skArc(sketch, "E322", {"start": v(-29.56, 53.88) * mm, "mid": v(-29.21, 57.89) * mm, "end": v(-28.89, 61.9) * mm});
            skArc(sketch, "E323", {"start": v(-27.95, 68.87) * mm, "mid": v(-28.58, 65.4) * mm, "end": v(-28.89, 61.9) * mm});
            skLineSegment(sketch, "E324", {"start": v(6.36, -64.57) * mm, "end": v(-1.07, -67.48) * mm});
            skArc(sketch, "E325", {"start": v(6.88, -66.35) * mm, "mid": v(6.97, -65.36) * mm, "end": v(6.36, -64.57) * mm});
            skArc(sketch, "E326", {"start": v(6.88, -66.35) * mm, "mid": v(6.25, -66.55) * mm, "end": v(5.75, -66.98) * mm});
            skArc(sketch, "E327", {"start": v(5.75, -66.98) * mm, "mid": v(5.55, -67.23) * mm, "end": v(5.53, -67.55) * mm});
            skArc(sketch, "E328", {"start": v(5.1, -67.92) * mm, "mid": v(5.41, -67.84) * mm, "end": v(5.53, -67.55) * mm});
            skArc(sketch, "E329", {"start": v(4.1, -67.55) * mm, "mid": v(4.55, -67.88) * mm, "end": v(5.1, -67.92) * mm});
            skArc(sketch, "E330", {"start": v(-1.07, -67.48) * mm, "mid": v(-1.16, -67.61) * mm, "end": v(-1.07, -67.75) * mm});
            skArc(sketch, "E331", {"start": v(4.1, -67.55) * mm, "mid": v(3.69, -67.57) * mm, "end": v(3.39, -67.85) * mm});
            skArc(sketch, "E332", {"start": v(1.8, -68.7) * mm, "mid": v(0.37, -68.22) * mm, "end": v(-1.07, -67.75) * mm});
            skArc(sketch, "E333", {"start": v(1.8, -68.7) * mm, "mid": v(2.33, -68.8) * mm, "end": v(2.84, -68.7) * mm});
            skArc(sketch, "E334", {"start": v(2.84, -68.7) * mm, "mid": v(3.2, -68.33) * mm, "end": v(3.39, -67.85) * mm});
            skArc(sketch, "E335", {"start": v(-2.57, -64.13) * mm, "mid": v(-2.7, -64.9) * mm, "end": v(-2.62, -65.68) * mm});
            skArc(sketch, "E336", {"start": v(-2.62, -65.68) * mm, "mid": v(-1.92, -66.23) * mm, "end": v(-1.02, -66.3) * mm});
            skArc(sketch, "E337", {"start": v(2.33, -64.77) * mm, "mid": v(0.6, -65.4) * mm, "end": v(-1.02, -66.3) * mm});
            skLineSegment(sketch, "E338", {"start": v(2.33, -64.77) * mm, "end": v(7.4, -63.07) * mm});
            skLineSegment(sketch, "E339", {"start": v(7.4, -63.07) * mm, "end": v(19.66, -60.09) * mm});
            skArc(sketch, "E340", {"start": v(19.66, -60.09) * mm, "mid": v(20.7, -59.64) * mm, "end": v(21.5, -58.86) * mm});
            skArc(sketch, "E341", {"start": v(21.5, -58.86) * mm, "mid": v(21.25, -58.02) * mm, "end": v(20.84, -57.23) * mm});
            skArc(sketch, "E342", {"start": v(21.88, -56.89) * mm, "mid": v(21.2, -56.6) * mm, "end": v(20.84, -57.23) * mm});
            skArc(sketch, "E343", {"start": v(22.44, -58.1) * mm, "mid": v(22.17, -57.49) * mm, "end": v(21.88, -56.89) * mm});
            skArc(sketch, "E344", {"start": v(22.44, -58.1) * mm, "mid": v(25.1, -57.54) * mm, "end": v(27.57, -56.4) * mm});
            skArc(sketch, "E345", {"start": v(27.57, -56.4) * mm, "mid": v(29.65, -54.79) * mm, "end": v(31.21, -52.68) * mm});
            skArc(sketch, "E346", {"start": v(31.21, -52.68) * mm, "mid": v(32.24, -49.66) * mm, "end": v(32.79, -46.52) * mm});
            skArc(sketch, "E347", {"start": v(32.79, -46.52) * mm, "mid": v(33.18, -43.12) * mm, "end": v(33.2, -39.7) * mm});
            skArc(sketch, "E348", {"start": v(33.2, -39.7) * mm, "mid": v(33.14, -37.11) * mm, "end": v(32.96, -34.53) * mm});
            skArc(sketch, "E349", {"start": v(32.96, -34.53) * mm, "mid": v(32.74, -31.97) * mm, "end": v(32.4, -29.43) * mm});
            skArc(sketch, "E350", {"start": v(32.4, -29.43) * mm, "mid": v(32.12, -27.5) * mm, "end": v(31.68, -25.61) * mm});
            skArc(sketch, "E351", {"start": v(25.08, -21.85) * mm, "mid": v(28.2, -24.06) * mm, "end": v(31.68, -25.61) * mm});
            skArc(sketch, "E352", {"start": v(25.08, -21.85) * mm, "mid": v(23.69, -20.44) * mm, "end": v(22.27, -19.06) * mm});
            skArc(sketch, "E353", {"start": v(22.27, -19.06) * mm, "mid": v(18.4, -21.25) * mm, "end": v(15.08, -24.21) * mm});
            skArc(sketch, "E354", {"start": v(15.08, -24.21) * mm, "mid": v(12.72, -26.78) * mm, "end": v(10.85, -29.73) * mm});
            skArc(sketch, "E355", {"start": v(10.85, -29.73) * mm, "mid": v(9.55, -32.49) * mm, "end": v(8.53, -35.37) * mm});
            skArc(sketch, "E356", {"start": v(8.53, -35.37) * mm, "mid": v(7.85, -38.11) * mm, "end": v(7.42, -40.9) * mm});
            skArc(sketch, "E357", {"start": v(7.42, -40.9) * mm, "mid": v(7.28, -44.23) * mm, "end": v(7.42, -47.56) * mm});
            skArc(sketch, "E358", {"start": v(7.42, -47.56) * mm, "mid": v(7.72, -49.17) * mm, "end": v(8.11, -50.76) * mm});
            skArc(sketch, "E359", {"start": v(8.11, -50.76) * mm, "mid": v(8.97, -51.49) * mm, "end": v(9.98, -51.96) * mm});
            skArc(sketch, "E360", {"start": v(9.37, -52.83) * mm, "mid": v(10.04, -52.66) * mm, "end": v(9.98, -51.96) * mm});
            skArc(sketch, "E361", {"start": v(7.55, -51.77) * mm, "mid": v(8.36, -52.47) * mm, "end": v(9.37, -52.83) * mm});
            skArc(sketch, "E362", {"start": v(3.9, -55.63) * mm, "mid": v(5.98, -53.94) * mm, "end": v(7.55, -51.77) * mm});
            skArc(sketch, "E363", {"start": v(-1.64, -57.92) * mm, "mid": v(1.18, -56.9) * mm, "end": v(3.9, -55.63) * mm});
            skArc(sketch, "E364", {"start": v(-1.64, -57.92) * mm, "mid": v(-2.99, -58.61) * mm, "end": v(-4.08, -59.67) * mm});
            skArc(sketch, "E365", {"start": v(-4.08, -59.67) * mm, "mid": v(-4.26, -60.27) * mm, "end": v(-4.25, -60.9) * mm});
            skArc(sketch, "E366", {"start": v(-3.44, -61.3) * mm, "mid": v(-3.82, -61.05) * mm, "end": v(-4.25, -60.9) * mm});
            skArc(sketch, "E367", {"start": v(-3.76, -62.23) * mm, "mid": v(-3.44, -61.82) * mm, "end": v(-3.44, -61.3) * mm});
            skArc(sketch, "E368", {"start": v(-3.76, -62.23) * mm, "mid": v(-4.1, -62.9) * mm, "end": v(-3.76, -63.56) * mm});
            skArc(sketch, "E369", {"start": v(-2.57, -64.13) * mm, "mid": v(-2.75, -63.92) * mm, "end": v(-3.02, -63.86) * mm});
            skArc(sketch, "E370", {"start": v(-3.76, -63.56) * mm, "mid": v(-3.42, -63.79) * mm, "end": v(-3.02, -63.86) * mm});
            skArc(sketch, "E371", {"start": v(-25.05, 68.75) * mm, "mid": v(-25.41, 68.47) * mm, "end": v(-25.51, 68.01) * mm});
            skArc(sketch, "E372", {"start": v(-24.36, 68.45) * mm, "mid": v(-24.66, 68.69) * mm, "end": v(-25.05, 68.75) * mm});
            skArc(sketch, "E373", {"start": v(-18.82, 63.33) * mm, "mid": v(-18.9, 63.57) * mm, "end": v(-19.13, 63.7) * mm});
            skArc(sketch, "E374", {"start": v(-19.12, 62.96) * mm, "mid": v(-18.92, 63.1) * mm, "end": v(-18.82, 63.33) * mm});
            skArc(sketch, "E375", {"start": v(-24.97, 60.66) * mm, "mid": v(-24.86, 60.49) * mm, "end": v(-24.65, 60.43) * mm});
            skLineSegment(sketch, "E376", {"start": v(-19.12, 62.95) * mm, "end": v(-21.93, 61.12) * mm});
            skLineSegment(sketch, "E377", {"start": v(-21.93, 61.12) * mm, "end": v(-24.65, 60.43) * mm});
            skArc(sketch, "E378", {"start": v(-25.28, 62.17) * mm, "mid": v(-25.16, 61.41) * mm, "end": v(-24.97, 60.66) * mm});
            skLineSegment(sketch, "E379", {"start": v(-25.28, 62.17) * mm, "end": v(-25.51, 68.01) * mm});
            skArc(sketch, "E380", {"start": v(-21.44, 65.98) * mm, "mid": v(-22.76, 67.38) * mm, "end": v(-24.36, 68.45) * mm});
            skArc(sketch, "E381", {"start": v(-19.13, 63.7) * mm, "mid": v(-20.28, 64.84) * mm, "end": v(-21.44, 65.98) * mm});
            skArc(sketch, "E382", {"start": v(-24.5, 67.56) * mm, "mid": v(-24.74, 67.47) * mm, "end": v(-24.77, 67.21) * mm});
            skArc(sketch, "E383", {"start": v(-24.1, 67.33) * mm, "mid": v(-24.26, 67.5) * mm, "end": v(-24.5, 67.56) * mm});
            skArc(sketch, "E384", {"start": v(-20.11, 63.32) * mm, "mid": v(-20.15, 63.55) * mm, "end": v(-20.27, 63.75) * mm});
            skArc(sketch, "E385", {"start": v(-20.36, 63.02) * mm, "mid": v(-20.18, 63.13) * mm, "end": v(-20.11, 63.32) * mm});
            skArc(sketch, "E386", {"start": v(-24.18, 61.39) * mm, "mid": v(-24.07, 61.15) * mm, "end": v(-23.82, 61.1) * mm});
            skArc(sketch, "E387", {"start": v(-23.82, 61.1) * mm, "mid": v(-23.48, 61.17) * mm, "end": v(-23.22, 61.38) * mm});
            skLineSegment(sketch, "E388", {"start": v(-20.36, 63.02) * mm, "end": v(-23.22, 61.38) * mm});
            skLineSegment(sketch, "E389", {"start": v(-24.77, 67.21) * mm, "end": v(-24.18, 61.39) * mm});
            skLineSegment(sketch, "E390", {"start": v(-20.27, 63.75) * mm, "end": v(-24.1, 67.33) * mm});
            skLineSegment(sketch, "E391", {"start": v(24.7, 64.4) * mm, "end": v(21, 60.81) * mm});
            skLineSegment(sketch, "E392", {"start": v(21, 59.92) * mm, "end": v(24.51, 58.72) * mm});
            skLineSegment(sketch, "E393", {"start": v(25.11, 58.99) * mm, "end": v(25.28, 64.17) * mm});
            skLineSegment(sketch, "E394", {"start": v(21, 60.81) * mm, "end": v(20.6, 60.43) * mm});
            skArc(sketch, "E395", {"start": v(20.6, 60.43) * mm, "mid": v(20.72, 60.12) * mm, "end": v(21, 59.92) * mm});
            skArc(sketch, "E396", {"start": v(24.51, 58.72) * mm, "mid": v(24.9, 58.66) * mm, "end": v(25.11, 58.99) * mm});
            skArc(sketch, "E397", {"start": v(25.28, 64.17) * mm, "mid": v(25.07, 64.49) * mm, "end": v(24.7, 64.4) * mm});
            skArc(sketch, "E398", {"start": v(19.86, 60.82) * mm, "mid": v(19.52, 60.34) * mm, "end": v(19.94, 59.92) * mm});
            skArc(sketch, "E399", {"start": v(25.67, 57.81) * mm, "mid": v(25.95, 57.85) * mm, "end": v(25.95, 58.13) * mm});
            skArc(sketch, "E400", {"start": v(26.14, 64.94) * mm, "mid": v(25.74, 65.68) * mm, "end": v(24.91, 65.53) * mm});
            skLineSegment(sketch, "E401", {"start": v(26.14, 64.94) * mm, "end": v(25.95, 58.13) * mm});
            skLineSegment(sketch, "E402", {"start": v(25.67, 57.81) * mm, "end": v(19.94, 59.92) * mm});
            skLineSegment(sketch, "E403", {"start": v(24.91, 65.53) * mm, "end": v(19.86, 60.82) * mm});
            skLineSegment(sketch, "E404", {"start": v(8.41, 46.77) * mm, "end": v(5.5, 45.46) * mm});
            skLineSegment(sketch, "E405", {"start": v(5.5, 45.46) * mm, "end": v(8.56, 44.32) * mm});
            skLineSegment(sketch, "E406", {"start": v(8.56, 44.32) * mm, "end": v(8.41, 46.77) * mm});
            skLineSegment(sketch, "E407", {"start": v(9.86, 47.02) * mm, "end": v(9.86, 44.32) * mm});
            skLineSegment(sketch, "E408", {"start": v(13.07, 45.85) * mm, "end": v(9.86, 47.02) * mm});
            skLineSegment(sketch, "E409", {"start": v(13.07, 45.85) * mm, "end": v(9.86, 44.32) * mm});
            skLineSegment(sketch, "E410", {"start": v(-8.88, 48.28) * mm, "end": v(-9.1, 46.14) * mm});
            skArc(sketch, "E411", {"start": v(-8.88, 48.28) * mm, "mid": v(-8.97, 48.5) * mm, "end": v(-9.21, 48.55) * mm});
            skLineSegment(sketch, "E412", {"start": v(-9.21, 48.55) * mm, "end": v(-11.37, 48.18) * mm});
            skArc(sketch, "E413", {"start": v(-11.37, 48.18) * mm, "mid": v(-11.62, 48.02) * mm, "end": v(-11.69, 47.72) * mm});
            skArc(sketch, "E414", {"start": v(-11.69, 47.72) * mm, "mid": v(-10.87, 46.76) * mm, "end": v(-9.85, 46.01) * mm});
            skArc(sketch, "E415", {"start": v(-9.85, 46.01) * mm, "mid": v(-9.45, 45.94) * mm, "end": v(-9.1, 46.14) * mm});
            skArc(sketch, "E416", {"start": v(-7.07, 48.15) * mm, "mid": v(-7.38, 48.15) * mm, "end": v(-7.57, 47.91) * mm});
            skArc(sketch, "E417", {"start": v(-5.2, 45.47) * mm, "mid": v(-4.9, 45.72) * mm, "end": v(-5.03, 46.08) * mm});
            skArc(sketch, "E418", {"start": v(-7.87, 45.86) * mm, "mid": v(-7.75, 45.6) * mm, "end": v(-7.49, 45.47) * mm});
            skLineSegment(sketch, "E419", {"start": v(-7.57, 47.91) * mm, "end": v(-7.87, 45.86) * mm});
            skLineSegment(sketch, "E420", {"start": v(-7.49, 45.47) * mm, "end": v(-5.2, 45.47) * mm});
            skArc(sketch, "E421", {"start": v(-5.03, 46.08) * mm, "mid": v(-5.86, 47.3) * mm, "end": v(-7.07, 48.15) * mm});
            skArc(sketch, "E422", {"start": v(-7.05, 47.87) * mm, "mid": v(-7.23, 47.92) * mm, "end": v(-7.32, 47.76) * mm});
            skArc(sketch, "E423", {"start": v(-5.48, 45.8) * mm, "mid": v(-5.26, 45.96) * mm, "end": v(-5.39, 46.2) * mm});
            skArc(sketch, "E424", {"start": v(-7.54, 46.15) * mm, "mid": v(-7.53, 45.92) * mm, "end": v(-7.33, 45.8) * mm});
            skLineSegment(sketch, "E425", {"start": v(-5.48, 45.8) * mm, "end": v(-7.33, 45.8) * mm});
            skLineSegment(sketch, "E426", {"start": v(-7.54, 46.15) * mm, "end": v(-7.32, 47.76) * mm});
            skArc(sketch, "E427", {"start": v(-5.39, 46.2) * mm, "mid": v(-6.11, 47.14) * mm, "end": v(-7.05, 47.87) * mm});
            skArc(sketch, "E428", {"start": v(-3.64, 44.76) * mm, "mid": v(-4.02, 47.6) * mm, "end": v(-6.37, 49.23) * mm});
            skArc(sketch, "E429", {"start": v(-12.43, 49.23) * mm, "mid": v(-13.28, 48.81) * mm, "end": v(-13.3, 47.87) * mm});
            skArc(sketch, "E430", {"start": v(-6.37, 49.23) * mm, "mid": v(-9.4, 49.77) * mm, "end": v(-12.43, 49.23) * mm});
            skArc(sketch, "E431", {"start": v(-13.3, 47.87) * mm, "mid": v(-11.8, 45.83) * mm, "end": v(-9.55, 44.66) * mm});
            skArc(sketch, "E432", {"start": v(-9.55, 44.66) * mm, "mid": v(-7.3, 44.6) * mm, "end": v(-5.07, 44.66) * mm});
            skArc(sketch, "E433", {"start": v(-4.1, 43.95) * mm, "mid": v(-4.54, 44.36) * mm, "end": v(-5.07, 44.66) * mm});
            skArc(sketch, "E434", {"start": v(-9.28, 48.22) * mm, "mid": v(-10.21, 48.13) * mm, "end": v(-11.11, 47.87) * mm});
            skArc(sketch, "E435", {"start": v(-9.4, 46.3) * mm, "mid": v(-9.27, 47.26) * mm, "end": v(-9.28, 48.22) * mm});
            skArc(sketch, "E436", {"start": v(-11.11, 47.87) * mm, "mid": v(-11.22, 47.78) * mm, "end": v(-11.23, 47.64) * mm});
            skArc(sketch, "E437", {"start": v(-9.93, 46.46) * mm, "mid": v(-9.69, 46.3) * mm, "end": v(-9.4, 46.3) * mm});
            skArc(sketch, "E438", {"start": v(-11.23, 47.64) * mm, "mid": v(-10.64, 47) * mm, "end": v(-9.94, 46.48) * mm});
            skArc(sketch, "E439", {"start": v(-2.23, 43.06) * mm, "mid": v(-2.74, 44.08) * mm, "end": v(-3.64, 44.76) * mm});
            skArc(sketch, "E440", {"start": v(-4, 43.74) * mm, "mid": v(-4.04, 43.85) * mm, "end": v(-4.1, 43.95) * mm});
            skArc(sketch, "E441", {"start": v(-2.85, 42.11) * mm, "mid": v(-2.39, 42.5) * mm, "end": v(-2.23, 43.06) * mm});
            skArc(sketch, "E442", {"start": v(-4, 43.64) * mm, "mid": v(-3.98, 43.01) * mm, "end": v(-3.68, 42.46) * mm});
            skArc(sketch, "E443", {"start": v(-3.67, 42.43) * mm, "mid": v(-3.3, 42.16) * mm, "end": v(-2.85, 42.11) * mm});
            skArc(sketch, "E444", {"start": v(2.63, 41.67) * mm, "mid": v(3.17, 40.94) * mm, "end": v(3.95, 41.41) * mm});
            skArc(sketch, "E445", {"start": v(2.7, 44.11) * mm, "mid": v(2.63, 42.9) * mm, "end": v(2.6, 41.67) * mm});
            skArc(sketch, "E446", {"start": v(4.12, 45.16) * mm, "mid": v(3.3, 44.8) * mm, "end": v(2.7, 44.11) * mm});
            skArc(sketch, "E447", {"start": v(4.64, 46.16) * mm, "mid": v(4.35, 45.92) * mm, "end": v(4.12, 45.61) * mm});
            skArc(sketch, "E448", {"start": v(4.12, 45.16) * mm, "mid": v(4.14, 45.39) * mm, "end": v(4.12, 45.61) * mm});
            skArc(sketch, "E449", {"start": v(8.43, 48.06) * mm, "mid": v(6.36, 47.45) * mm, "end": v(4.64, 46.16) * mm});
            skArc(sketch, "E450", {"start": v(13.13, 47.46) * mm, "mid": v(10.83, 48.12) * mm, "end": v(8.43, 48.06) * mm});
            skArc(sketch, "E451", {"start": v(14.78, 45.84) * mm, "mid": v(14.08, 46.77) * mm, "end": v(13.13, 47.46) * mm});
            skArc(sketch, "E452", {"start": v(11.74, 43.67) * mm, "mid": v(13.44, 44.5) * mm, "end": v(14.78, 45.84) * mm});
            skArc(sketch, "E453", {"start": v(7.98, 43.43) * mm, "mid": v(9.87, 43.32) * mm, "end": v(11.74, 43.67) * mm});
            skArc(sketch, "E454", {"start": v(5.28, 44.2) * mm, "mid": v(6.6, 43.68) * mm, "end": v(7.98, 43.43) * mm});
            skArc(sketch, "E455", {"start": v(4.12, 43.43) * mm, "mid": v(4.72, 43.78) * mm, "end": v(5.28, 44.2) * mm});
            skLineSegment(sketch, "E456", {"start": v(3.95, 41.41) * mm, "end": v(3.95, 43.26) * mm});
            skArc(sketch, "E457", {"start": v(4.12, 43.43) * mm, "mid": v(4, 43.38) * mm, "end": v(3.95, 43.26) * mm});
            skArc(sketch, "E458", {"start": v(8.24, 46.17) * mm, "mid": v(8.07, 46.33) * mm, "end": v(7.85, 46.27) * mm});
            skArc(sketch, "E459", {"start": v(6.72, 45.76) * mm, "mid": v(6.42, 45.54) * mm, "end": v(6.67, 45.26) * mm});
            skArc(sketch, "E460", {"start": v(7.77, 44.92) * mm, "mid": v(8.08, 44.85) * mm, "end": v(8.28, 45.1) * mm});
            skArc(sketch, "E461", {"start": v(10.57, 46.47) * mm, "mid": v(10.28, 46.54) * mm, "end": v(10.14, 46.27) * mm});
            skArc(sketch, "E462", {"start": v(10.16, 45.23) * mm, "mid": v(10.32, 44.96) * mm, "end": v(10.63, 45) * mm});
            skArc(sketch, "E463", {"start": v(11.94, 45.66) * mm, "mid": v(12.09, 45.8) * mm, "end": v(11.93, 45.93) * mm});
            skLineSegment(sketch, "E464", {"start": v(11.93, 45.93) * mm, "end": v(10.57, 46.47) * mm});
            skLineSegment(sketch, "E465", {"start": v(10.14, 46.27) * mm, "end": v(10.16, 45.23) * mm});
            skLineSegment(sketch, "E466", {"start": v(11.94, 45.66) * mm, "end": v(10.63, 45) * mm});
            skLineSegment(sketch, "E467", {"start": v(7.77, 44.92) * mm, "end": v(6.67, 45.26) * mm});
            skLineSegment(sketch, "E468", {"start": v(7.85, 46.27) * mm, "end": v(6.72, 45.76) * mm});
            skLineSegment(sketch, "E469", {"start": v(8.24, 46.17) * mm, "end": v(8.28, 45.1) * mm});
            skArc(sketch, "E470", {"start": v(3.08, 39.35) * mm, "mid": v(0.62, 40.04) * mm, "end": v(-1.95, 40.07) * mm});
            skArc(sketch, "E471", {"start": v(3.83, 37.81) * mm, "mid": v(3.88, 38.8) * mm, "end": v(3.04, 39.33) * mm});
            skArc(sketch, "E472", {"start": v(-1.95, 40.07) * mm, "mid": v(-2.72, 39.71) * mm, "end": v(-2.94, 38.9) * mm});
            skLineSegment(sketch, "E473", {"start": v(-2.94, 38.9) * mm, "end": v(-0.97, 35.8) * mm});
            skLineSegment(sketch, "E474", {"start": v(3.83, 37.81) * mm, "end": v(1.3, 35.57) * mm});
            skArc(sketch, "E475", {"start": v(-1.57, 38.72) * mm, "mid": v(-0.92, 37.28) * mm, "end": v(0.08, 36.07) * mm});
            skArc(sketch, "E476", {"start": v(0.08, 36.07) * mm, "mid": v(1.2, 36.93) * mm, "end": v(2.2, 37.95) * mm});
            skArc(sketch, "E477", {"start": v(2.23, 38.15) * mm, "mid": v(0.38, 38.73) * mm, "end": v(-1.57, 38.72) * mm});
            skArc(sketch, "E478", {"start": v(2.2, 37.95) * mm, "mid": v(2.23, 38.05) * mm, "end": v(2.23, 38.15) * mm});
            skLineSegment(sketch, "E479", {"start": v(-0.56, 35.28) * mm, "end": v(-0.97, 35.8) * mm});
            skLineSegment(sketch, "E480", {"start": v(1.3, 35.57) * mm, "end": v(0.8, 34.94) * mm});
            skArc(sketch, "E481", {"start": v(0.8, 34.94) * mm, "mid": v(0.69, 33.92) * mm, "end": v(1.26, 33.06) * mm});
            skArc(sketch, "E482", {"start": v(-1.06, 33.63) * mm, "mid": v(-0.56, 34.38) * mm, "end": v(-0.56, 35.28) * mm});
            skArc(sketch, "E483", {"start": v(1.26, 33.06) * mm, "mid": v(2.14, 32.57) * mm, "end": v(3.13, 32.36) * mm});
            skArc(sketch, "E484", {"start": v(8.83, 34.44) * mm, "mid": v(8.46, 35.22) * mm, "end": v(7.85, 35.83) * mm});
            skArc(sketch, "E485", {"start": v(8.13, 32.94) * mm, "mid": v(8.7, 33.58) * mm, "end": v(8.83, 34.44) * mm});
            skLineSegment(sketch, "E486", {"start": v(3.13, 32.36) * mm, "end": v(7.52, 32.55) * mm});
            skArc(sketch, "E487", {"start": v(7.52, 32.55) * mm, "mid": v(7.88, 32.66) * mm, "end": v(8.13, 32.94) * mm});
            skArc(sketch, "E488", {"start": v(8.22, 36.27) * mm, "mid": v(7.84, 36.22) * mm, "end": v(7.85, 35.83) * mm});
            skArc(sketch, "E489", {"start": v(10.08, 34.09) * mm, "mid": v(9.43, 35.41) * mm, "end": v(8.22, 36.27) * mm});
            skArc(sketch, "E490", {"start": v(8.66, 31.47) * mm, "mid": v(9.7, 32.6) * mm, "end": v(10.08, 34.09) * mm});
            skArc(sketch, "E491", {"start": v(7.54, 31.2) * mm, "mid": v(8.1, 31.29) * mm, "end": v(8.66, 31.47) * mm});
            skArc(sketch, "E492", {"start": v(0, 32.57) * mm, "mid": v(-0.87, 32.5) * mm, "end": v(-1.62, 32.07) * mm});
            skArc(sketch, "E493", {"start": v(0.47, 32.41) * mm, "mid": v(0.24, 32.5) * mm, "end": v(0, 32.57) * mm});
            skArc(sketch, "E494", {"start": v(2.23, 31.26) * mm, "mid": v(1.36, 31.85) * mm, "end": v(0.47, 32.41) * mm});
            skArc(sketch, "E495", {"start": v(2.23, 31.26) * mm, "mid": v(4.88, 31.05) * mm, "end": v(7.54, 31.2) * mm});
            skArc(sketch, "E496", {"start": v(-4.1, 32.07) * mm, "mid": v(-2.86, 31.9) * mm, "end": v(-1.62, 32.07) * mm});
            skArc(sketch, "E497", {"start": v(-7.4, 32.97) * mm, "mid": v(-5.76, 32.5) * mm, "end": v(-4.1, 32.07) * mm});
            skArc(sketch, "E498", {"start": v(-9.31, 34.7) * mm, "mid": v(-8.59, 33.58) * mm, "end": v(-7.4, 32.97) * mm});
            skArc(sketch, "E499", {"start": v(-9.31, 35.81) * mm, "mid": v(-9.45, 35.26) * mm, "end": v(-9.31, 34.7) * mm});
            skArc(sketch, "E500", {"start": v(-8.11, 35.67) * mm, "mid": v(-8.67, 36.14) * mm, "end": v(-9.31, 35.81) * mm});
            skArc(sketch, "E501", {"start": v(-8.11, 35.67) * mm, "mid": v(-7.63, 34.5) * mm, "end": v(-6.51, 33.88) * mm});
            skArc(sketch, "E502", {"start": v(-6.5, 33.91) * mm, "mid": v(-4.81, 33.44) * mm, "end": v(-3.08, 33.18) * mm});
            skArc(sketch, "E503", {"start": v(-3.08, 33.18) * mm, "mid": v(-2.02, 33.2) * mm, "end": v(-1.06, 33.63) * mm});
            skArc(sketch, "E504", {"start": v(-4.75, 30.12) * mm, "mid": v(-4.85, 29.36) * mm, "end": v(-4.63, 28.63) * mm});
            skArc(sketch, "E505", {"start": v(-4.63, 28.63) * mm, "mid": v(-4.1, 28.02) * mm, "end": v(-3.3, 27.86) * mm});
            skArc(sketch, "E506", {"start": v(-2.86, 27.61) * mm, "mid": v(-3, 27.85) * mm, "end": v(-3.28, 27.86) * mm});
            skArc(sketch, "E507", {"start": v(-2.86, 27.61) * mm, "mid": v(-2.5, 27.4) * mm, "end": v(-2.14, 27.6) * mm});
            skArc(sketch, "E508", {"start": v(-1.3, 27.4) * mm, "mid": v(-1.68, 27.68) * mm, "end": v(-2.14, 27.6) * mm});
            skArc(sketch, "E509", {"start": v(-1.3, 27.4) * mm, "mid": v(-0.79, 27.08) * mm, "end": v(-0.22, 27.26) * mm});
            skArc(sketch, "E510", {"start": v(0.3, 27.2) * mm, "mid": v(0.83, 27) * mm, "end": v(1.23, 27.4) * mm});
            skArc(sketch, "E511", {"start": v(0.3, 27.2) * mm, "mid": v(0.09, 27.3) * mm, "end": v(-0.15, 27.28) * mm});
            skArc(sketch, "E512", {"start": v(2.29, 27.82) * mm, "mid": v(1.68, 27.83) * mm, "end": v(1.23, 27.4) * mm});
            skArc(sketch, "E513", {"start": v(3.74, 29.13) * mm, "mid": v(2.95, 28.55) * mm, "end": v(2.29, 27.82) * mm});
            skArc(sketch, "E514", {"start": v(3.74, 29.13) * mm, "mid": v(3.51, 29.52) * mm, "end": v(3.06, 29.54) * mm});
            skArc(sketch, "E515", {"start": v(-4, 29.81) * mm, "mid": v(-4.3, 30.15) * mm, "end": v(-4.75, 30.12) * mm});
            skArc(sketch, "E516", {"start": v(3.06, 29.54) * mm, "mid": v(2.2, 28.96) * mm, "end": v(1.38, 28.32) * mm});
            skArc(sketch, "E517", {"start": v(-4, 29.81) * mm, "mid": v(-1.49, 28.45) * mm, "end": v(1.38, 28.32) * mm});
            skCircle(sketch, "E518", {"center": v(-6.34, 36.27) * mm, "radius": 0.49 * mm});
            skCircle(sketch, "E519", {"center": v(-4.66, 35.23) * mm, "radius": 0.35 * mm});
            skCircle(sketch, "E520", {"center": v(3.9, 34.04) * mm, "radius": 0.37 * mm});
            skCircle(sketch, "E521", {"center": v(6.37, 34.96) * mm, "radius": 0.35 * mm});
            skSolve(sketch);
        }
        {
            var Q0;
            Q0=sQuery(id+"F0.wireOp",EDGE,"E361");
            var Q1;
            Q1=sQuery(id+"F0.wireOp",EDGE,"E41");
            var Q2;
            Q2=sQuery(id+"F0.wireOp",EDGE,"E121");
            var Q3;
            Q3=sQuery(id+"F0.wireOp",EDGE,"E490");
            var Q4;
            Q4=sQuery(id+"F0.wireOp",EDGE,"E170");
            var Q5;
            Q5=sQuery(id+"F0.wireOp",EDGE,"E491");
            var Q6;
            Q6=sQuery(id+"F0.wireOp",EDGE,"E59");
            var Q7;
            Q7=sQuery(id+"F0.wireOp",EDGE,"E188");
            var Q8;
            Q8=sQuery(id+"F0.wireOp",EDGE,"E172");
            var Q9;
            Q9=sQuery(id+"F0.wireOp",EDGE,"E364");
            var Q10;
            Q10=sQuery(id+"F0.wireOp",EDGE,"E428");
            var Q11;
            Q11=sQuery(id+"F0.wireOp",EDGE,"E381");
            var Q12;
            Q12=sQuery(id+"F0.wireOp",EDGE,"E77");
            var Q13;
            Q13=sQuery(id+"F0.wireOp",EDGE,"E286");
            var Q14;
            Q14=sQuery(id+"F0.wireOp",EDGE,"E158");
            var Q15;
            Q15=sQuery(id+"F0.wireOp",EDGE,"E207");
            var Q16;
            Q16=sQuery(id+"F0.wireOp",EDGE,"E159");
            var Q17;
            Q17=sQuery(id+"F0.wireOp",EDGE,"E48");
            var Q18;
            Q18=sQuery(id+"F0.wireOp",EDGE,"E176");
            var Q19;
            Q19=sQuery(id+"F0.wireOp",EDGE,"E497");
            var Q20;
            Q20=sQuery(id+"F0.wireOp",EDGE,"E513");
            var Q21;
            Q21=sQuery(id+"F0.wireOp",EDGE,"E65");
            var Q22;
            Q22=sQuery(id+"F0.wireOp",EDGE,"E145");
            var Q23;
            Q23=sQuery(id+"F0.wireOp",EDGE,"E97");
            var Q24;
            Q24=sQuery(id+"F0.wireOp",EDGE,"E273");
            var Q25;
            Q25=sQuery(id+"F0.wireOp",EDGE,"E241");
            var Q26;
            Q26=sQuery(id+"F0.wireOp",EDGE,"E289");
            var Q27;
            Q27=sQuery(id+"F0.wireOp",EDGE,"E18");
            var Q28;
            Q28=sQuery(id+"F0.wireOp",EDGE,"E146");
            var Q29;
            Q29=sQuery(id+"F0.wireOp",EDGE,"E98");
            var Q30;
            Q30=sQuery(id+"F0.wireOp",EDGE,"E338");
            var Q31;
            Q31=sQuery(id+"F0.wireOp",EDGE,"E228");
            var Q32;
            Q32=sQuery(id+"F0.wireOp",EDGE,"E276");
            var Q33;
            Q33=sQuery(id+"F0.wireOp",EDGE,"E340");
            var Q34;
            Q34=sQuery(id+"F0.wireOp",EDGE,"E229");
            var Q35;
            Q35=sQuery(id+"F0.wireOp",EDGE,"E341");
            var Q36;
            Q36=sQuery(id+"F0.wireOp",EDGE,"E182");
            var Q37;
            Q37=sQuery(id+"F0.wireOp",EDGE,"E166");
            var Q38;
            Q38=sQuery(id+"F0.wireOp",EDGE,"E342");
            var Q39;
            Q39=sQuery(id+"F0.wireOp",EDGE,"E486");
            var Q40;
            Q40=sQuery(id+"F0.wireOp",EDGE,"E167");
            var Q41;
            Q41=sQuery(id+"F0.wireOp",EDGE,"E135");
            var Q42;
            Q42=sQuery(id+"F0.wireOp",EDGE,"E231");
            var Q43;
            Q43=sQuery(id+"F0.wireOp",EDGE,"E359");
            var Q44;
            Q44=sQuery(id+"F0.wireOp",EDGE,"E343");
            var Q45;
            Q45=sQuery(id+"F0.wireOp",EDGE,"E519");
            var Q46;
            Q46=sQuery(id+"F0.wireOp",EDGE,"E503");
            var Q47;
            Q47=sQuery(id+"F0.wireOp",EDGE,"E487");
            var Q48;
            Q48=sQuery(id+"F0.wireOp",EDGE,"E120");
            var Q49;
            Q49=sQuery(id+"F0.wireOp",EDGE,"E360");
            var Q50;
            Q50=sQuery(id+"F0.wireOp",EDGE,"E489");
            var Q51;
            Q51=sQuery(id+"F0.wireOp",EDGE,"E521");
            var Q52;
            Q52=sQuery(id+"F0.wireOp",EDGE,"E249");
            var Q53;
            Q53=sQuery(id+"F0.wireOp",EDGE,"E217");
            var Q54;
            Q54=sQuery(id+"F0.wireOp",EDGE,"E297");
            var Q55;
            Q55=sQuery(id+"F0.wireOp",EDGE,"E90");
            var Q56;
            Q56=sQuery(id+"F0.wireOp",EDGE,"E443");
            var Q57;
            Q57=sQuery(id+"F0.wireOp",EDGE,"E299");
            var Q58;
            Q58=sQuery(id+"F0.wireOp",EDGE,"E300");
            var Q59;
            Q59=sQuery(id+"F0.wireOp",EDGE,"E396");
            var Q60;
            Q60=sQuery(id+"F0.wireOp",EDGE,"E380");
            var Q61;
            Q61=sQuery(id+"F0.wireOp",EDGE,"E237");
            var Q62;
            Q62=sQuery(id+"F0.wireOp",EDGE,"E397");
            var Q63;
            Q63=sQuery(id+"F0.wireOp",EDGE,"E365");
            var Q64;
            Q64=sQuery(id+"F0.wireOp",EDGE,"E477");
            var Q65;
            Q65=sQuery(id+"F0.wireOp",EDGE,"E494");
            var Q66;
            Q66=sQuery(id+"F0.wireOp",EDGE,"E399");
            var Q67;
            Q67=sQuery(id+"F0.wireOp",EDGE,"E175");
            var Q68;
            Q68=sQuery(id+"F0.wireOp",EDGE,"E400");
            var Q69;
            Q69=sQuery(id+"F0.wireOp",EDGE,"E496");
            var Q70;
            Q70=sQuery(id+"F0.wireOp",EDGE,"E512");
            var Q71;
            Q71=sQuery(id+"F0.wireOp",EDGE,"E17");
            var Q72;
            Q72=sQuery(id+"F0.wireOp",EDGE,"E177");
            var Q73;
            Q73=sQuery(id+"F0.wireOp",EDGE,"E225");
            var Q74;
            Q74=sQuery(id+"F0.wireOp",EDGE,"E450");
            var Q75;
            Q75=sQuery(id+"F0.wireOp",EDGE,"E178");
            var Q76;
            Q76=sQuery(id+"F0.wireOp",EDGE,"E258");
            var Q77;
            Q77=sQuery(id+"F0.wireOp",EDGE,"E242");
            var Q78;
            Q78=sQuery(id+"F0.wireOp",EDGE,"E226");
            var Q79;
            Q79=sQuery(id+"F0.wireOp",EDGE,"E402");
            var Q80;
            Q80=sQuery(id+"F0.wireOp",EDGE,"E147");
            var Q81;
            Q81=sQuery(id+"F0.wireOp",EDGE,"E227");
            var Q82;
            Q82=sQuery(id+"F0.wireOp",EDGE,"E195");
            var Q83;
            Q83=sQuery(id+"F0.wireOp",EDGE,"E259");
            var Q84;
            Q84=sQuery(id+"F0.wireOp",EDGE,"E483");
            var Q85;
            Q85=sQuery(id+"F0.wireOp",EDGE,"E180");
            var Q86;
            Q86=sQuery(id+"F0.wireOp",EDGE,"E148");
            var Q87;
            Q87=sQuery(id+"F0.wireOp",EDGE,"E260");
            var Q88;
            Q88=sQuery(id+"F0.wireOp",EDGE,"E324");
            var Q89;
            Q89=sQuery(id+"F0.wireOp",EDGE,"E516");
            var Q90;
            Q90=sQuery(id+"F0.wireOp",EDGE,"E484");
            var Q91;
            Q91=sQuery(id+"F0.wireOp",EDGE,"E181");
            var Q92;
            Q92=sQuery(id+"F0.wireOp",EDGE,"E165");
            var Q93;
            Q93=sQuery(id+"F0.wireOp",EDGE,"E261");
            var Q94;
            Q94=sQuery(id+"F0.wireOp",EDGE,"E517");
            var Q95;
            Q95=sQuery(id+"F0.wireOp",EDGE,"E485");
            var Q96;
            Q96=sQuery(id+"F0.wireOp",EDGE,"E230");
            var Q97;
            Q97=sQuery(id+"F0.wireOp",EDGE,"E262");
            var Q98;
            Q98=sQuery(id+"F0.wireOp",EDGE,"E470");
            var Q99;
            Q99=sQuery(id+"F0.wireOp",EDGE,"E151");
            var Q100;
            Q100=sQuery(id+"F0.wireOp",EDGE,"E391");
            var Q101;
            Q101=sQuery(id+"F0.wireOp",EDGE,"E439");
            var Q102;
            Q102=sQuery(id+"F0.wireOp",EDGE,"E232");
            var Q103;
            Q103=sQuery(id+"F0.wireOp",EDGE,"E296");
            var Q104;
            Q104=sQuery(id+"F0.wireOp",EDGE,"E408");
            var Q105;
            Q105=sQuery(id+"F0.wireOp",EDGE,"E392");
            var Q106;
            Q106=sQuery(id+"F0.wireOp",EDGE,"E472");
            var Q107;
            Q107=sQuery(id+"F0.wireOp",EDGE,"E520");
            var Q108;
            Q108=sQuery(id+"F0.wireOp",EDGE,"E504");
            var Q109;
            Q109=sQuery(id+"F0.wireOp",EDGE,"E488");
            var Q110;
            Q110=sQuery(id+"F0.wireOp",EDGE,"E377");
            var Q111;
            Q111=sQuery(id+"F0.wireOp",EDGE,"E409");
            var Q112;
            Q112=sQuery(id+"F0.wireOp",EDGE,"E473");
            var Q113;
            Q113=sQuery(id+"F0.wireOp",EDGE,"E441");
            var Q114;
            Q114=sQuery(id+"F0.wireOp",EDGE,"E505");
            var Q115;
            Q115=sQuery(id+"F0.wireOp",EDGE,"E89");
            var Q116;
            Q116=sQuery(id+"F0.wireOp",EDGE,"E169");
            var Q117;
            Q117=sQuery(id+"F0.wireOp",EDGE,"E442");
            var Q118;
            Q118=sQuery(id+"F0.wireOp",EDGE,"E26");
            var Q119;
            Q119=sQuery(id+"F0.wireOp",EDGE,"E298");
            var Q120;
            Q120=sQuery(id+"F0.wireOp",EDGE,"E282");
            var Q121;
            Q121=sQuery(id+"F0.wireOp",EDGE,"E378");
            var Q122;
            Q122=sQuery(id+"F0.wireOp",EDGE,"E475");
            var Q123;
            Q123=sQuery(id+"F0.wireOp",EDGE,"E27");
            var Q124;
            Q124=sQuery(id+"F0.wireOp",EDGE,"E155");
            var Q125;
            Q125=sQuery(id+"F0.wireOp",EDGE,"E235");
            var Q126;
            Q126=sQuery(id+"F0.wireOp",EDGE,"E395");
            var Q127;
            Q127=sQuery(id+"F0.wireOp",EDGE,"E236");
            var Q128;
            Q128=sQuery(id+"F0.wireOp",EDGE,"E332");
            var Q129;
            Q129=sQuery(id+"F0.wireOp",EDGE,"E492");
            var Q130;
            Q130=sQuery(id+"F0.wireOp",EDGE,"E173");
            var Q131;
            Q131=sQuery(id+"F0.wireOp",EDGE,"E157");
            var Q132;
            Q132=sQuery(id+"F0.wireOp",EDGE,"E333");
            var Q133;
            Q133=sQuery(id+"F0.wireOp",EDGE,"E493");
            var Q134;
            Q134=sQuery(id+"F0.wireOp",EDGE,"E398");
            var Q135;
            Q135=sQuery(id+"F0.wireOp",EDGE,"E366");
            var Q136;
            Q136=sQuery(id+"F0.wireOp",EDGE,"E510");
            var Q137;
            Q137=sQuery(id+"F0.wireOp",EDGE,"E174");
            var Q138;
            Q138=sQuery(id+"F0.wireOp",EDGE,"E335");
            var Q139;
            Q139=sQuery(id+"F0.wireOp",EDGE,"E367");
            var Q140;
            Q140=sQuery(id+"F0.wireOp",EDGE,"E431");
            var Q141;
            Q141=sQuery(id+"F0.wireOp",EDGE,"E368");
            var Q142;
            Q142=sQuery(id+"F0.wireOp",EDGE,"E16");
            var Q143;
            Q143=sQuery(id+"F0.wireOp",EDGE,"E80");
            var Q144;
            Q144=sQuery(id+"F0.wireOp",EDGE,"E160");
            var Q145;
            Q145=sQuery(id+"F0.wireOp",EDGE,"E336");
            var Q146;
            Q146=sQuery(id+"F0.wireOp",EDGE,"E481");
            var Q147;
            Q147=sQuery(id+"F0.wireOp",EDGE,"E81");
            var Q148;
            Q148=sQuery(id+"F0.wireOp",EDGE,"E369");
            var Q149;
            Q149=sQuery(id+"F0.wireOp",EDGE,"E482");
            var Q150;
            Q150=sQuery(id+"F0.wireOp",EDGE,"E82");
            var Q151;
            Q151=sQuery(id+"F0.wireOp",EDGE,"E162");
            var Q152;
            Q152=sQuery(id+"F0.wireOp",EDGE,"E274");
            var Q153;
            Q153=sQuery(id+"F0.wireOp",EDGE,"E370");
            var Q154;
            Q154=sQuery(id+"F0.wireOp",EDGE,"E83");
            var Q155;
            Q155=sQuery(id+"F0.wireOp",EDGE,"E275");
            var Q156;
            Q156=sQuery(id+"F0.wireOp",EDGE,"E387");
            var Q157;
            Q157=sQuery(id+"F0.wireOp",EDGE,"E515");
            var Q158;
            Q158=sQuery(id+"F0.wireOp",EDGE,"E388");
            var Q159;
            Q159=sQuery(id+"F0.wireOp",EDGE,"E373");
            var Q160;
            Q160=sQuery(id+"F0.wireOp",EDGE,"E453");
            var Q161;
            Q161=sQuery(id+"F0.wireOp",EDGE,"E390");
            var Q162;
            Q162=sQuery(id+"F0.wireOp",EDGE,"E375");
            var Q163;
            Q163=sQuery(id+"F0.wireOp",EDGE,"E152");
            var Q164;
            Q164=sQuery(id+"F0.wireOp",EDGE,"E280");
            var Q165;
            Q165=sQuery(id+"F0.wireOp",EDGE,"E264");
            var Q166;
            Q166=sQuery(id+"F0.wireOp",EDGE,"E376");
            var Q167;
            Q167=sQuery(id+"F0.wireOp",EDGE,"E185");
            var Q168;
            Q168=sQuery(id+"F0.wireOp",EDGE,"E265");
            var Q169;
            Q169=sQuery(id+"F0.wireOp",EDGE,"E233");
            var Q170;
            Q170=sQuery(id+"F0.wireOp",EDGE,"E281");
            var Q171;
            Q171=sQuery(id+"F0.wireOp",EDGE,"E474");
            var Q172;
            Q172=sQuery(id+"F0.wireOp",EDGE,"E506");
            var Q173;
            Q173=sQuery(id+"F0.wireOp",EDGE,"E186");
            var Q174;
            Q174=sQuery(id+"F0.wireOp",EDGE,"E154");
            var Q175;
            Q175=sQuery(id+"F0.wireOp",EDGE,"E234");
            var Q176;
            Q176=sQuery(id+"F0.wireOp",EDGE,"E330");
            var Q177;
            Q177=sQuery(id+"F0.wireOp",EDGE,"E394");
            var Q178;
            Q178=sQuery(id+"F0.wireOp",EDGE,"E91");
            var Q179;
            Q179=sQuery(id+"F0.wireOp",EDGE,"E187");
            var Q180;
            Q180=sQuery(id+"F0.wireOp",EDGE,"E156");
            var Q181;
            Q181=sQuery(id+"F0.wireOp",EDGE,"E476");
            var Q182;
            Q182=sQuery(id+"F0.wireOp",EDGE,"E508");
            var Q183;
            Q183=sQuery(id+"F0.wireOp",EDGE,"E301");
            var Q184;
            Q184=sQuery(id+"F0.wireOp",EDGE,"E285");
            var Q185;
            Q185=sQuery(id+"F0.wireOp",EDGE,"E445");
            var Q186;
            Q186=sQuery(id+"F0.wireOp",EDGE,"E509");
            var Q187;
            Q187=sQuery(id+"F0.wireOp",EDGE,"E430");
            var Q188;
            Q188=sQuery(id+"F0.wireOp",EDGE,"E478");
            var Q189;
            Q189=sQuery(id+"F0.wireOp",EDGE,"E446");
            var Q190;
            Q190=sQuery(id+"F0.wireOp",EDGE,"E94");
            var Q191;
            Q191=sQuery(id+"F0.wireOp",EDGE,"E287");
            var Q192;
            Q192=sQuery(id+"F0.wireOp",EDGE,"E479");
            var Q193;
            Q193=sQuery(id+"F0.wireOp",EDGE,"E447");
            var Q194;
            Q194=sQuery(id+"F0.wireOp",EDGE,"E511");
            var Q195;
            Q195=sQuery(id+"F0.wireOp",EDGE,"E384");
            var Q196;
            Q196=sQuery(id+"F0.wireOp",EDGE,"E480");
            var Q197;
            Q197=sQuery(id+"F0.wireOp",EDGE,"E448");
            var Q198;
            Q198=sQuery(id+"F0.wireOp",EDGE,"E33");
            var Q199;
            Q199=sQuery(id+"F0.wireOp",EDGE,"E161");
            var Q200;
            Q200=sQuery(id+"F0.wireOp",EDGE,"E385");
            var Q201;
            Q201=sQuery(id+"F0.wireOp",EDGE,"E34");
            var Q202;
            Q202=sQuery(id+"F0.wireOp",EDGE,"E386");
            var Q203;
            Q203=sQuery(id+"F0.wireOp",EDGE,"E291");
            var Q204;
            Q204=sQuery(id+"F0.wireOp",EDGE,"E292");
            var Q205;
            Q205=sQuery(id+"F0.wireOp",EDGE,"E37");
            var Q206;
            Q206=sQuery(id+"F0.wireOp",EDGE,"E293");
            var Q207;
            Q207=sQuery(id+"F0.wireOp",EDGE,"E325");
            var Q208;
            Q208=sQuery(id+"F0.wireOp",EDGE,"E150");
            var Q209;
            Q209=sQuery(id+"F0.wireOp",EDGE,"E374");
            var Q210;
            Q210=sQuery(id+"F0.wireOp",EDGE,"E326");
            var Q211;
            Q211=sQuery(id+"F0.wireOp",EDGE,"E295");
            var Q212;
            Q212=sQuery(id+"F0.wireOp",EDGE,"E263");
            var Q213;
            Q213=sQuery(id+"F0.wireOp",EDGE,"E407");
            var Q214;
            Q214=sQuery(id+"F0.wireOp",EDGE,"E471");
            var Q215;
            Q215=sQuery(id+"F0.wireOp",EDGE,"E72");
            var Q216;
            Q216=sQuery(id+"F0.wireOp",EDGE,"E136");
            var Q217;
            Q217=sQuery(id+"F0.wireOp",EDGE,"E456");
            var Q218;
            Q218=sQuery(id+"F0.wireOp",EDGE,"E153");
            var Q219;
            Q219=sQuery(id+"F0.wireOp",EDGE,"E507");
            var Q220;
            Q220=sQuery(id+"F0.wireOp",EDGE,"E411");
            var Q221;
            Q221=sQuery(id+"F0.wireOp",EDGE,"E92");
            var Q222;
            Q222=sQuery(id+"F0.wireOp",EDGE,"E444");
            var Q223;
            Q223=sQuery(id+"F0.wireOp",EDGE,"E28");
            var Q224;
            Q224=sQuery(id+"F0.wireOp",EDGE,"E334");
            var Q225;
            Q225=sQuery(id+"F0.wireOp",EDGE,"E302");
            var Q226;
            Q226=sQuery(id+"F0.wireOp",EDGE,"E30");
            var Q227;
            Q227=sQuery(id+"F0.wireOp",EDGE,"E303");
            var Q228;
            Q228=sQuery(id+"F0.wireOp",EDGE,"E383");
            var Q229;
            Q229=sQuery(id+"F0.wireOp",EDGE,"E31");
            var Q230;
            Q230=sQuery(id+"F0.wireOp",EDGE,"E464");
            var Q231;
            Q231=sQuery(id+"F0.wireOp",EDGE,"E32");
            var Q232;
            Q232=sQuery(id+"F0.wireOp",EDGE,"E256");
            var Q233;
            Q233=sQuery(id+"F0.wireOp",EDGE,"E304");
            var Q234;
            Q234=sQuery(id+"F0.wireOp",EDGE,"E465");
            var Q235;
            Q235=sQuery(id+"F0.wireOp",EDGE,"E449");
            var Q236;
            Q236=sQuery(id+"F0.wireOp",EDGE,"E257");
            var Q237;
            Q237=sQuery(id+"F0.wireOp",EDGE,"E305");
            var Q238;
            Q238=sQuery(id+"F0.wireOp",EDGE,"E466");
            var Q239;
            Q239=sQuery(id+"F0.wireOp",EDGE,"E306");
            var Q240;
            Q240=sQuery(id+"F0.wireOp",EDGE,"E290");
            var Q241;
            Q241=sQuery(id+"F0.wireOp",EDGE,"E371");
            var Q242;
            Q242=sQuery(id+"F0.wireOp",EDGE,"E36");
            var Q243;
            Q243=sQuery(id+"F0.wireOp",EDGE,"E372");
            var Q244;
            Q244=sQuery(id+"F0.wireOp",EDGE,"E149");
            var Q245;
            Q245=sQuery(id+"F0.wireOp",EDGE,"E421");
            var Q246;
            Q246=sQuery(id+"F0.wireOp",EDGE,"E294");
            var Q247;
            Q247=sQuery(id+"F0.wireOp",EDGE,"E327");
            var Q248;
            Q248=sQuery(id+"F0.wireOp",EDGE,"E455");
            var Q249;
            Q249=sQuery(id+"F0.wireOp",EDGE,"E328");
            var Q250;
            Q250=sQuery(id+"F0.wireOp",EDGE,"E457");
            var Q251;
            Q251=sQuery(id+"F0.wireOp",EDGE,"E329");
            var Q252;
            Q252=sQuery(id+"F0.wireOp",EDGE,"E410");
            var Q253;
            Q253=sQuery(id+"F0.wireOp",EDGE,"E331");
            var Q254;
            Q254=sQuery(id+"F0.wireOp",EDGE,"E461");
            var Q255;
            Q255=sQuery(id+"F0.wireOp",EDGE,"E29");
            var Q256;
            Q256=sQuery(id+"F0.wireOp",EDGE,"E382");
            var Q257;
            Q257=sQuery(id+"F0.wireOp",EDGE,"E462");
            var Q258;
            Q258=sQuery(id+"F0.wireOp",EDGE,"E463");
            var Q259;
            Q259=sQuery(id+"F0.wireOp",EDGE,"E416");
            var Q260;
            Q260=sQuery(id+"F0.wireOp",EDGE,"E35");
            var Q261;
            Q261=sQuery(id+"F0.wireOp",EDGE,"E138");
            var Q262;
            Q262=sQuery(id+"F0.wireOp",EDGE,"E139");
            var Q263;
            Q263=sQuery(id+"F0.wireOp",EDGE,"E143");
            var Q264;
            Q264=sQuery(id+"F0.wireOp",EDGE,"E144");
            var Q265;
            Q265=sQuery(id+"F0.wireOp",EDGE,"E183");
            var Q266;
            Q266=sQuery(id+"F0.wireOp",EDGE,"E184");
            var Q267;
            Q267=sQuery(id+"F0.wireOp",EDGE,"E440");
            var Q268;
            Q268=sQuery(id+"F0.wireOp",EDGE,"E137");
            var Q269;
            Q269=sQuery(id+"F0.wireOp",EDGE,"E427");
            var Q270;
            Q270=sQuery(id+"F0.wireOp",EDGE,"E429");
            var Q271;
            Q271=sQuery(id+"F0.wireOp",EDGE,"E413");
            var Q272;
            Q272=sQuery(id+"F0.wireOp",EDGE,"E141");
            var Q273;
            Q273=sQuery(id+"F0.wireOp",EDGE,"E414");
            var Q274;
            Q274=sQuery(id+"F0.wireOp",EDGE,"E142");
            var Q275;
            Q275=sQuery(id+"F0.wireOp",EDGE,"E432");
            var Q276;
            Q276=sQuery(id+"F0.wireOp",EDGE,"E433");
            var Q277;
            Q277=sQuery(id+"F0.wireOp",EDGE,"E434");
            var Q278;
            Q278=sQuery(id+"F0.wireOp",EDGE,"E418");
            var Q279;
            Q279=sQuery(id+"F0.wireOp",EDGE,"E467");
            var Q280;
            Q280=sQuery(id+"F0.wireOp",EDGE,"E435");
            var Q281;
            Q281=sQuery(id+"F0.wireOp",EDGE,"E419");
            var Q282;
            Q282=sQuery(id+"F0.wireOp",EDGE,"E468");
            var Q283;
            Q283=sQuery(id+"F0.wireOp",EDGE,"E420");
            var Q284;
            Q284=sQuery(id+"F0.wireOp",EDGE,"E405");
            var Q285;
            Q285=sQuery(id+"F0.wireOp",EDGE,"E469");
            var Q286;
            Q286=sQuery(id+"F0.wireOp",EDGE,"E406");
            var Q287;
            Q287=sQuery(id+"F0.wireOp",EDGE,"E454");
            var Q288;
            Q288=sQuery(id+"F0.wireOp",EDGE,"E438");
            var Q289;
            Q289=sQuery(id+"F0.wireOp",EDGE,"E422");
            var Q290;
            Q290=sQuery(id+"F0.wireOp",EDGE,"E423");
            var Q291;
            Q291=sQuery(id+"F0.wireOp",EDGE,"E424");
            var Q292;
            Q292=sQuery(id+"F0.wireOp",EDGE,"E425");
            var Q293;
            Q293=sQuery(id+"F0.wireOp",EDGE,"E426");
            var Q294;
            Q294=sQuery(id+"F0.wireOp",EDGE,"E458");
            var Q295;
            Q295=sQuery(id+"F0.wireOp",EDGE,"E459");
            var Q296;
            Q296=sQuery(id+"F0.wireOp",EDGE,"E140");
            var Q297;
            Q297=sQuery(id+"F0.wireOp",EDGE,"E412");
            var Q298;
            Q298=sQuery(id+"F0.wireOp",EDGE,"E460");
            var Q299;
            Q299=sQuery(id+"F0.wireOp",EDGE,"E417");
            var Q300;
            Q300=sQuery(id+"F0.wireOp",EDGE,"E404");
            var Q301;
            Q301=sQuery(id+"F0.wireOp",EDGE,"E436");
            var Q302;
            Q302=sQuery(id+"F0.wireOp",EDGE,"E437");
            var Q303;
            Q303=sQuery(id+"F0.wireOp",EDGE,"E415");
            var Q304;
            Q304=sQuery(id+"F0.wireOp",EDGE,"E201");
            var Q305;
            Q305=sQuery(id+"F0.wireOp",EDGE,"E218");
            var Q306;
            Q306=sQuery(id+"F0.wireOp",EDGE,"E203");
            var Q307;
            Q307=sQuery(id+"F0.wireOp",EDGE,"E219");
            var Q308;
            Q308=sQuery(id+"F0.wireOp",EDGE,"E220");
            var Q309;
            Q309=sQuery(id+"F0.wireOp",EDGE,"E221");
            var Q310;
            Q310=sQuery(id+"F0.wireOp",EDGE,"E349");
            var Q311;
            Q311=sQuery(id+"F0.wireOp",EDGE,"E350");
            var Q312;
            Q312=sQuery(id+"F0.wireOp",EDGE,"E126");
            var Q313;
            Q313=sQuery(id+"F0.wireOp",EDGE,"E351");
            var Q314;
            Q314=sQuery(id+"F0.wireOp",EDGE,"E47");
            var Q315;
            Q315=sQuery(id+"F0.wireOp",EDGE,"E353");
            var Q316;
            Q316=sQuery(id+"F0.wireOp",EDGE,"E354");
            var Q317;
            Q317=sQuery(id+"F0.wireOp",EDGE,"E355");
            var Q318;
            Q318=sQuery(id+"F0.wireOp",EDGE,"E212");
            var Q319;
            Q319=sQuery(id+"F0.wireOp",EDGE,"E196");
            var Q320;
            Q320=sQuery(id+"F0.wireOp",EDGE,"E356");
            var Q321;
            Q321=sQuery(id+"F0.wireOp",EDGE,"E213");
            var Q322;
            Q322=sQuery(id+"F0.wireOp",EDGE,"E197");
            var Q323;
            Q323=sQuery(id+"F0.wireOp",EDGE,"E357");
            var Q324;
            Q324=sQuery(id+"F0.wireOp",EDGE,"E215");
            var Q325;
            Q325=sQuery(id+"F0.wireOp",EDGE,"E216");
            var Q326;
            Q326=sQuery(id+"F0.wireOp",EDGE,"E200");
            var Q327;
            Q327=sQuery(id+"F0.wireOp",EDGE,"E347");
            var Q328;
            Q328=sQuery(id+"F0.wireOp",EDGE,"E202");
            var Q329;
            Q329=sQuery(id+"F0.wireOp",EDGE,"E348");
            var Q330;
            Q330=sQuery(id+"F0.wireOp",EDGE,"E125");
            var Q331;
            Q331=sQuery(id+"F0.wireOp",EDGE,"E222");
            var Q332;
            Q332=sQuery(id+"F0.wireOp",EDGE,"E223");
            var Q333;
            Q333=sQuery(id+"F0.wireOp",EDGE,"E352");
            var Q334;
            Q334=sQuery(id+"F0.wireOp",EDGE,"E210");
            var Q335;
            Q335=sQuery(id+"F0.wireOp",EDGE,"E211");
            var Q336;
            Q336=sQuery(id+"F0.wireOp",EDGE,"E214");
            var Q337;
            Q337=sQuery(id+"F0.wireOp",EDGE,"E198");
            var Q338;
            Q338=sQuery(id+"F0.wireOp",EDGE,"E199");
            var Q339;
            Q339=sQuery(id+"F0.wireOp",EDGE,"E313");
            var Q340;
            Q340=sQuery(id+"F0.wireOp",EDGE,"E123");
            var Q341;
            Q341=sQuery(id+"F0.wireOp",EDGE,"E251");
            var Q342;
            Q342=sQuery(id+"F0.wireOp",EDGE,"E283");
            var Q343;
            Q343=sQuery(id+"F0.wireOp",EDGE,"E252");
            var Q344;
            Q344=sQuery(id+"F0.wireOp",EDGE,"E284");
            var Q345;
            Q345=sQuery(id+"F0.wireOp",EDGE,"E60");
            var Q346;
            Q346=sQuery(id+"F0.wireOp",EDGE,"E253");
            var Q347;
            Q347=sQuery(id+"F0.wireOp",EDGE,"E254");
            var Q348;
            Q348=sQuery(id+"F0.wireOp",EDGE,"E271");
            var Q349;
            Q349=sQuery(id+"F0.wireOp",EDGE,"E192");
            var Q350;
            Q350=sQuery(id+"F0.wireOp",EDGE,"E130");
            var Q351;
            Q351=sQuery(id+"F0.wireOp",EDGE,"E115");
            var Q352;
            Q352=sQuery(id+"F0.wireOp",EDGE,"E179");
            var Q353;
            Q353=sQuery(id+"F0.wireOp",EDGE,"E163");
            var Q354;
            Q354=sQuery(id+"F0.wireOp",EDGE,"E116");
            var Q355;
            Q355=sQuery(id+"F0.wireOp",EDGE,"E164");
            var Q356;
            Q356=sQuery(id+"F0.wireOp",EDGE,"E117");
            var Q357;
            Q357=sQuery(id+"F0.wireOp",EDGE,"E309");
            var Q358;
            Q358=sQuery(id+"F0.wireOp",EDGE,"E118");
            var Q359;
            Q359=sQuery(id+"F0.wireOp",EDGE,"E310");
            var Q360;
            Q360=sQuery(id+"F0.wireOp",EDGE,"E119");
            var Q361;
            Q361=sQuery(id+"F0.wireOp",EDGE,"E311");
            var Q362;
            Q362=sQuery(id+"F0.wireOp",EDGE,"E168");
            var Q363;
            Q363=sQuery(id+"F0.wireOp",EDGE,"E312");
            var Q364;
            Q364=sQuery(id+"F0.wireOp",EDGE,"E270");
            var Q365;
            Q365=sQuery(id+"F0.wireOp",EDGE,"E57");
            var Q366;
            Q366=sQuery(id+"F0.wireOp",EDGE,"E58");
            var Q367;
            Q367=sQuery(id+"F0.wireOp",EDGE,"E122");
            var Q368;
            Q368=sQuery(id+"F0.wireOp",EDGE,"E171");
            var Q369;
            Q369=sQuery(id+"F0.wireOp",EDGE,"E267");
            var Q370;
            Q370=sQuery(id+"F0.wireOp",EDGE,"E124");
            var Q371;
            Q371=sQuery(id+"F0.wireOp",EDGE,"E268");
            var Q372;
            Q372=sQuery(id+"F0.wireOp",EDGE,"E189");
            var Q373;
            Q373=sQuery(id+"F0.wireOp",EDGE,"E190");
            var Q374;
            Q374=sQuery(id+"F0.wireOp",EDGE,"E127");
            var Q375;
            Q375=sQuery(id+"F0.wireOp",EDGE,"E191");
            var Q376;
            Q376=sQuery(id+"F0.wireOp",EDGE,"E255");
            var Q377;
            Q377=sQuery(id+"F0.wireOp",EDGE,"E128");
            var Q378;
            Q378=sQuery(id+"F0.wireOp",EDGE,"E272");
            var Q379;
            Q379=sQuery(id+"F0.wireOp",EDGE,"E288");
            var Q380;
            Q380=sQuery(id+"F0.wireOp",EDGE,"E129");
            var Q381;
            Q381=sQuery(id+"F0.wireOp",EDGE,"E193");
            var Q382;
            Q382=sQuery(id+"F0.wireOp",EDGE,"E194");
            var Q383;
            Q383=sQuery(id+"F0.wireOp",EDGE,"E131");
            var Q384;
            Q384=sQuery(id+"F0.wireOp",EDGE,"E132");
            var Q385;
            Q385=sQuery(id+"F0.wireOp",EDGE,"E308");
            var Q386;
            Q386=sQuery(id+"F0.wireOp",EDGE,"E133");
            var Q387;
            Q387=sQuery(id+"F0.wireOp",EDGE,"E277");
            var Q388;
            Q388=sQuery(id+"F0.wireOp",EDGE,"E134");
            var Q389;
            Q389=sQuery(id+"F0.wireOp",EDGE,"E278");
            var Q390;
            Q390=sQuery(id+"F0.wireOp",EDGE,"E55");
            var Q391;
            Q391=sQuery(id+"F0.wireOp",EDGE,"E279");
            var Q392;
            Q392=sQuery(id+"F0.wireOp",EDGE,"E56");
            var Q393;
            Q393=sQuery(id+"F0.wireOp",EDGE,"E266");
            var Q394;
            Q394=sQuery(id+"F0.wireOp",EDGE,"E269");
            var Q395;
            Q395=sQuery(id+"F0.wireOp",EDGE,"E307");
            var Q396;
            Q396=sQuery(id+"F0.wireOp",EDGE,"E250");
            var Q397;
            Q397=sQuery(id+"F0.wireOp",EDGE,"E314");
            var Q398;
            Q398=sQuery(id+"F0.wireOp",EDGE,"E315");
            var Q399;
            Q399=sQuery(id+"F0.wireOp",EDGE,"E316");
            var Q400;
            Q400=sQuery(id+"F0.wireOp",EDGE,"E317");
            var Q401;
            Q401=sQuery(id+"F0.wireOp",EDGE,"E318");
            var Q402;
            Q402=sQuery(id+"F0.wireOp",EDGE,"E244");
            var Q403;
            Q403=sQuery(id+"F0.wireOp",EDGE,"E245");
            var Q404;
            Q404=sQuery(id+"F0.wireOp",EDGE,"E246");
            var Q405;
            Q405=sQuery(id+"F0.wireOp",EDGE,"E247");
            var Q406;
            Q406=sQuery(id+"F0.wireOp",EDGE,"E248");
            var Q407;
            Q407=sQuery(id+"F0.wireOp",EDGE,"E9");
            var Q408;
            Q408=sQuery(id+"F0.wireOp",EDGE,"E10");
            var Q409;
            Q409=sQuery(id+"F0.wireOp",EDGE,"E4");
            var Q410;
            Q410=sQuery(id+"F0.wireOp",EDGE,"E5");
            var Q411;
            Q411=sQuery(id+"F0.wireOp",EDGE,"E6");
            var Q412;
            Q412=sQuery(id+"F0.wireOp",EDGE,"E7");
            var Q413;
            Q413=sQuery(id+"F0.wireOp",EDGE,"E8");
            var Q414;
            Q414=sQuery(id+"F0.wireOp",EDGE,"E12");
            var Q415;
            Q415=sQuery(id+"F0.wireOp",EDGE,"E13");
            var Q416;
            Q416=sQuery(id+"F0.wireOp",EDGE,"E14");
            var Q417;
            Q417=sQuery(id+"F0.wireOp",EDGE,"E319");
            var Q418;
            Q418=sQuery(id+"F0.wireOp",EDGE,"E11");
            var Q419;
            Q419=sQuery(id+"F0.wireOp",EDGE,"E393");
            var Q420;
            Q420=sQuery(id+"F0.wireOp",EDGE,"E73");
            var Q421;
            Q421=sQuery(id+"F0.wireOp",EDGE,"E105");
            var Q422;
            Q422=sQuery(id+"F0.wireOp",EDGE,"E74");
            var Q423;
            Q423=sQuery(id+"F0.wireOp",EDGE,"E75");
            var Q424;
            Q424=sQuery(id+"F0.wireOp",EDGE,"E107");
            var Q425;
            Q425=sQuery(id+"F0.wireOp",EDGE,"E379");
            var Q426;
            Q426=sQuery(id+"F0.wireOp",EDGE,"E76");
            var Q427;
            Q427=sQuery(id+"F0.wireOp",EDGE,"E61");
            var Q428;
            Q428=sQuery(id+"F0.wireOp",EDGE,"E93");
            var Q429;
            Q429=sQuery(id+"F0.wireOp",EDGE,"E78");
            var Q430;
            Q430=sQuery(id+"F0.wireOp",EDGE,"E62");
            var Q431;
            Q431=sQuery(id+"F0.wireOp",EDGE,"E110");
            var Q432;
            Q432=sQuery(id+"F0.wireOp",EDGE,"E495");
            var Q433;
            Q433=sQuery(id+"F0.wireOp",EDGE,"E79");
            var Q434;
            Q434=sQuery(id+"F0.wireOp",EDGE,"E63");
            var Q435;
            Q435=sQuery(id+"F0.wireOp",EDGE,"E111");
            var Q436;
            Q436=sQuery(id+"F0.wireOp",EDGE,"E95");
            var Q437;
            Q437=sQuery(id+"F0.wireOp",EDGE,"E320");
            var Q438;
            Q438=sQuery(id+"F0.wireOp",EDGE,"E321");
            var Q439;
            Q439=sQuery(id+"F0.wireOp",EDGE,"E401");
            var Q440;
            Q440=sQuery(id+"F0.wireOp",EDGE,"E322");
            var Q441;
            Q441=sQuery(id+"F0.wireOp",EDGE,"E323");
            var Q442;
            Q442=sQuery(id+"F0.wireOp",EDGE,"E403");
            var Q443;
            Q443=sQuery(id+"F0.wireOp",EDGE,"E84");
            var Q444;
            Q444=sQuery(id+"F0.wireOp",EDGE,"E452");
            var Q445;
            Q445=sQuery(id+"F0.wireOp",EDGE,"E85");
            var Q446;
            Q446=sQuery(id+"F0.wireOp",EDGE,"E389");
            var Q447;
            Q447=sQuery(id+"F0.wireOp",EDGE,"E86");
            var Q448;
            Q448=sQuery(id+"F0.wireOp",EDGE,"E70");
            var Q449;
            Q449=sQuery(id+"F0.wireOp",EDGE,"E87");
            var Q450;
            Q450=sQuery(id+"F0.wireOp",EDGE,"E71");
            var Q451;
            Q451=sQuery(id+"F0.wireOp",EDGE,"E0");
            var Q452;
            Q452=sQuery(id+"F0.wireOp",EDGE,"E1");
            var Q453;
            Q453=sQuery(id+"F0.wireOp",EDGE,"E2");
            var Q454;
            Q454=sQuery(id+"F0.wireOp",EDGE,"E3");
            var Q455;
            Q455=sQuery(id+"F0.wireOp",EDGE,"E106");
            var Q456;
            Q456=sQuery(id+"F0.wireOp",EDGE,"E108");
            var Q457;
            Q457=sQuery(id+"F0.wireOp",EDGE,"E109");
            var Q458;
            Q458=sQuery(id+"F0.wireOp",EDGE,"E64");
            var Q459;
            Q459=sQuery(id+"F0.wireOp",EDGE,"E112");
            var Q460;
            Q460=sQuery(id+"F0.wireOp",EDGE,"E96");
            var Q461;
            Q461=sQuery(id+"F0.wireOp",EDGE,"E113");
            var Q462;
            Q462=sQuery(id+"F0.wireOp",EDGE,"E498");
            var Q463;
            Q463=sQuery(id+"F0.wireOp",EDGE,"E66");
            var Q464;
            Q464=sQuery(id+"F0.wireOp",EDGE,"E114");
            var Q465;
            Q465=sQuery(id+"F0.wireOp",EDGE,"E99");
            var Q466;
            Q466=sQuery(id+"F0.wireOp",EDGE,"E67");
            var Q467;
            Q467=sQuery(id+"F0.wireOp",EDGE,"E451");
            var Q468;
            Q468=sQuery(id+"F0.wireOp",EDGE,"E100");
            var Q469;
            Q469=sQuery(id+"F0.wireOp",EDGE,"E68");
            var Q470;
            Q470=sQuery(id+"F0.wireOp",EDGE,"E101");
            var Q471;
            Q471=sQuery(id+"F0.wireOp",EDGE,"E69");
            var Q472;
            Q472=sQuery(id+"F0.wireOp",EDGE,"E501");
            var Q473;
            Q473=sQuery(id+"F0.wireOp",EDGE,"E102");
            var Q474;
            Q474=sQuery(id+"F0.wireOp",EDGE,"E518");
            var Q475;
            Q475=sQuery(id+"F0.wireOp",EDGE,"E502");
            var Q476;
            Q476=sQuery(id+"F0.wireOp",EDGE,"E103");
            var Q477;
            Q477=sQuery(id+"F0.wireOp",EDGE,"E104");
            var Q478;
            Q478=sQuery(id+"F0.wireOp",EDGE,"E88");
            var Q479;
            Q479=sQuery(id+"F0.wireOp",EDGE,"E514");
            var Q480;
            Q480=sQuery(id+"F0.wireOp",EDGE,"E499");
            var Q481;
            Q481=sQuery(id+"F0.wireOp",EDGE,"E500");
            var Q482;
            Q482=sQuery(id+"F0.wireOp",EDGE,"E345");
            var Q483;
            Q483=sQuery(id+"F0.wireOp",EDGE,"E25");
            var Q484;
            Q484=sQuery(id+"F0.wireOp",EDGE,"E42");
            var Q485;
            Q485=sQuery(id+"F0.wireOp",EDGE,"E363");
            var Q486;
            Q486=sQuery(id+"F0.wireOp",EDGE,"E44");
            var Q487;
            Q487=sQuery(id+"F0.wireOp",EDGE,"E238");
            var Q488;
            Q488=sQuery(id+"F0.wireOp",EDGE,"E206");
            var Q489;
            Q489=sQuery(id+"F0.wireOp",EDGE,"E209");
            var Q490;
            Q490=sQuery(id+"F0.wireOp",EDGE,"E243");
            var Q491;
            Q491=sQuery(id+"F0.wireOp",EDGE,"E339");
            var Q492;
            Q492=sQuery(id+"F0.wireOp",EDGE,"E38");
            var Q493;
            Q493=sQuery(id+"F0.wireOp",EDGE,"E39");
            var Q494;
            Q494=sQuery(id+"F0.wireOp",EDGE,"E24");
            var Q495;
            Q495=sQuery(id+"F0.wireOp",EDGE,"E344");
            var Q496;
            Q496=sQuery(id+"F0.wireOp",EDGE,"E362");
            var Q497;
            Q497=sQuery(id+"F0.wireOp",EDGE,"E205");
            var Q498;
            Q498=sQuery(id+"F0.wireOp",EDGE,"E337");
            var Q499;
            Q499=sQuery(id+"F0.wireOp",EDGE,"E346");
            var Q500;
            Q500=sQuery(id+"F0.wireOp",EDGE,"E43");
            var Q501;
            Q501=sQuery(id+"F0.wireOp",EDGE,"E204");
            var Q502;
            Q502=sQuery(id+"F0.wireOp",EDGE,"E45");
            var Q503;
            Q503=sQuery(id+"F0.wireOp",EDGE,"E46");
            var Q504;
            Q504=sQuery(id+"F0.wireOp",EDGE,"E15");
            var Q505;
            Q505=sQuery(id+"F0.wireOp",EDGE,"E239");
            var Q506;
            Q506=sQuery(id+"F0.wireOp",EDGE,"E208");
            var Q507;
            Q507=sQuery(id+"F0.wireOp",EDGE,"E240");
            var Q508;
            Q508=sQuery(id+"F0.wireOp",EDGE,"E224");
            var Q509;
            Q509=sQuery(id+"F0.wireOp",EDGE,"E19");
            var Q510;
            Q510=sQuery(id+"F0.wireOp",EDGE,"E20");
            var Q511;
            Q511=sQuery(id+"F0.wireOp",EDGE,"E21");
            var Q512;
            Q512=sQuery(id+"F0.wireOp",EDGE,"E22");
            var Q513;
            Q513=sQuery(id+"F0.wireOp",EDGE,"E358");
            var Q514;
            Q514=sQuery(id+"F0.wireOp",EDGE,"E23");
            var Q515;
            Q515=sQuery(id+"F0.wireOp",EDGE,"E40");
            var Q516;
            Q516=sQuery(id+"F0.wireOp",EDGE,"E54");
            var Q517;
            Q517=sQuery(id+"F0.wireOp",EDGE,"E49");
            var Q518;
            Q518=sQuery(id+"F0.wireOp",EDGE,"E50");
            var Q519;
            Q519=sQuery(id+"F0.wireOp",EDGE,"E51");
            var Q520;
            Q520=sQuery(id+"F0.wireOp",EDGE,"E52");
            var Q521;
            Q521=sQuery(id+"F0.wireOp",EDGE,"E53");
            extrude(context, id + "F1", {"bodyType" : ToolBodyType.SURFACE, "surfaceEntities" : qUnion([Q0, Q1, Q2, Q3, Q4, Q5, Q6, Q7, Q8, Q9, Q10, Q11, Q12, Q13, Q14, Q15, Q16, Q17, Q18, Q19, Q20, Q21, Q22, Q23, Q24, Q25, Q26, Q27, Q28, Q29, Q30, Q31, Q32, Q33, Q34, Q35, Q36, Q37, Q38, Q39, Q40, Q41, Q42, Q43, Q44, Q45, Q46, Q47, Q48, Q49, Q50, Q51, Q52, Q53, Q54, Q55, Q56, Q57, Q58, Q59, Q60, Q61, Q62, Q63, Q64, Q65, Q66, Q67, Q68, Q69, Q70, Q71, Q72, Q73, Q74, Q75, Q76, Q77, Q78, Q79, Q80, Q81, Q82, Q83, Q84, Q85, Q86, Q87, Q88, Q89, Q90, Q91, Q92, Q93, Q94, Q95, Q96, Q97, Q98, Q99, Q100, Q101, Q102, Q103, Q104, Q105, Q106, Q107, Q108, Q109, Q110, Q111, Q112, Q113, Q114, Q115, Q116, Q117, Q118, Q119, Q120, Q121, Q122, Q123, Q124, Q125, Q126, Q127, Q128, Q129, Q130, Q131, Q132, Q133, Q134, Q135, Q136, Q137, Q138, Q139, Q140, Q141, Q142, Q143, Q144, Q145, Q146, Q147, Q148, Q149, Q150, Q151, Q152, Q153, Q154, Q155, Q156, Q157, Q158, Q159, Q160, Q161, Q162, Q163, Q164, Q165, Q166, Q167, Q168, Q169, Q170, Q171, Q172, Q173, Q174, Q175, Q176, Q177, Q178, Q179, Q180, Q181, Q182, Q183, Q184, Q185, Q186, Q187, Q188, Q189, Q190, Q191, Q192, Q193, Q194, Q195, Q196, Q197, Q198, Q199, Q200, Q201, Q202, Q203, Q204, Q205, Q206, Q207, Q208, Q209, Q210, Q211, Q212, Q213, Q214, Q215, Q216, Q217, Q218, Q219, Q220, Q221, Q222, Q223, Q224, Q225, Q226, Q227, Q228, Q229, Q230, Q231, Q232, Q233, Q234, Q235, Q236, Q237, Q238, Q239, Q240, Q241, Q242, Q243, Q244, Q245, Q246, Q247, Q248, Q249, Q250, Q251, Q252, Q253, Q254, Q255, Q256, Q257, Q258, Q259, Q260, Q261, Q262, Q263, Q264, Q265, Q266, Q267, Q268, Q269, Q270, Q271, Q272, Q273, Q274, Q275, Q276, Q277, Q278, Q279, Q280, Q281, Q282, Q283, Q284, Q285, Q286, Q287, Q288, Q289, Q290, Q291, Q292, Q293, Q294, Q295, Q296, Q297, Q298, Q299, Q300, Q301, Q302, Q303, Q304, Q305, Q306, Q307, Q308, Q309, Q310, Q311, Q312, Q313, Q314, Q315, Q316, Q317, Q318, Q319, Q320, Q321, Q322, Q323, Q324, Q325, Q326, Q327, Q328, Q329, Q330, Q331, Q332, Q333, Q334, Q335, Q336, Q337, Q338, Q339, Q340, Q341, Q342, Q343, Q344, Q345, Q346, Q347, Q348, Q349, Q350, Q351, Q352, Q353, Q354, Q355, Q356, Q357, Q358, Q359, Q360, Q361, Q362, Q363, Q364, Q365, Q366, Q367, Q368, Q369, Q370, Q371, Q372, Q373, Q374, Q375, Q376, Q377, Q378, Q379, Q380, Q381, Q382, Q383, Q384, Q385, Q386, Q387, Q388, Q389, Q390, Q391, Q392, Q393, Q394, Q395, Q396, Q397, Q398, Q399, Q400, Q401, Q402, Q403, Q404, Q405, Q406, Q407, Q408, Q409, Q410, Q411, Q412, Q413, Q414, Q415, Q416, Q417, Q418, Q419, Q420, Q421, Q422, Q423, Q424, Q425, Q426, Q427, Q428, Q429, Q430, Q431, Q432, Q433, Q434, Q435, Q436, Q437, Q438, Q439, Q440, Q441, Q442, Q443, Q444, Q445, Q446, Q447, Q448, Q449, Q450, Q451, Q452, Q453, Q454, Q455, Q456, Q457, Q458, Q459, Q460, Q461, Q462, Q463, Q464, Q465, Q466, Q467, Q468, Q469, Q470, Q471, Q472, Q473, Q474, Q475, Q476, Q477, Q478, Q479, Q480, Q481, Q482, Q483, Q484, Q485, Q486, Q487, Q488, Q489, Q490, Q491, Q492, Q493, Q494, Q495, Q496, Q497, Q498, Q499, Q500, Q501, Q502, Q503, Q504, Q505, Q506, Q507, Q508, Q509, Q510, Q511, Q512, Q513, Q514, Q515, Q516, Q517, Q518, Q519, Q520, Q521]), "depth" : 19.05 * mm, "offsetDistance" : 25.4 * mm});
        }
        {
            var Q0;
            Q0=makeQuery(id+"F0.imprint","IMPRINT",FACE,{"disambiguationData":[TD([[makeQuery(id+"F0.imprint","IMPRINT",EDGE,{"derivedFrom":sQuery(id+"F0.wireOp",EDGE,"E335")}),1.0]])]});
            var Q1;
            Q1=makeQuery(id+"F0.imprint","IMPRINT",FACE,{"disambiguationData":[TD([[makeQuery(id+"F0.imprint","IMPRINT",EDGE,{"derivedFrom":sQuery(id+"F0.wireOp",EDGE,"E391")}),1.0]])]});
            var Q2;
            Q2=makeQuery(id+"F0.imprint","IMPRINT",FACE,{"disambiguationData":[TD([[makeQuery(id+"F0.imprint","IMPRINT",EDGE,{"derivedFrom":sQuery(id+"F0.wireOp",EDGE,"E382")}),1.0]])]});
            var Q3;
            Q3=makeQuery(id+"F0.imprint","IMPRINT",FACE,{"disambiguationData":[TD([[makeQuery(id+"F0.imprint","IMPRINT",EDGE,{"derivedFrom":sQuery(id+"F0.wireOp",EDGE,"E0")}),1.0]])]});
            var Q4;
            Q4=makeQuery(id+"F0.imprint","IMPRINT",FACE,{"disambiguationData":[TD([[makeQuery(id+"F0.imprint","IMPRINT",EDGE,{"derivedFrom":sQuery(id+"F0.wireOp",EDGE,"E324")}),1.0]])]});
            var Q5;
            Q5=makeQuery(id+"F0.imprint","IMPRINT",FACE,{"disambiguationData":[TD([[makeQuery(id+"F0.imprint","IMPRINT",EDGE,{"derivedFrom":sQuery(id+"F0.wireOp",EDGE,"E404")}),1.0]])]});
            var Q6;
            Q6=makeQuery(id+"F0.imprint","IMPRINT",FACE,{"disambiguationData":[TD([[makeQuery(id+"F0.imprint","IMPRINT",EDGE,{"derivedFrom":sQuery(id+"F0.wireOp",EDGE,"E407")}),1.0]])]});
            var Q7;
            Q7=makeQuery(id+"F0.imprint","IMPRINT",FACE,{"disambiguationData":[TD([[makeQuery(id+"F0.imprint","IMPRINT",EDGE,{"derivedFrom":sQuery(id+"F0.wireOp",EDGE,"E391")}),-1.0]])]});
            var Q8;
            Q8=makeQuery(id+"F0.imprint","IMPRINT",FACE,{"disambiguationData":[TD([[makeQuery(id+"F0.imprint","IMPRINT",EDGE,{"derivedFrom":sQuery(id+"F0.wireOp",EDGE,"E518")}),1.0]])]});
            var Q9;
            Q9=makeQuery(id+"F0.imprint","IMPRINT",FACE,{"disambiguationData":[TD([[makeQuery(id+"F0.imprint","IMPRINT",EDGE,{"derivedFrom":sQuery(id+"F0.wireOp",EDGE,"E519")}),1.0]])]});
            var Q10;
            Q10=makeQuery(id+"F0.imprint","IMPRINT",FACE,{"disambiguationData":[TD([[makeQuery(id+"F0.imprint","IMPRINT",EDGE,{"derivedFrom":sQuery(id+"F0.wireOp",EDGE,"E520")}),1.0]])]});
            var Q11;
            Q11=makeQuery(id+"F0.imprint","IMPRINT",FACE,{"disambiguationData":[TD([[makeQuery(id+"F0.imprint","IMPRINT",EDGE,{"derivedFrom":sQuery(id+"F0.wireOp",EDGE,"E521")}),1.0]])]});
            var Q12;
            Q12=makeQuery(id+"F0.imprint","IMPRINT",FACE,{"disambiguationData":[TD([[makeQuery(id+"F0.imprint","IMPRINT",EDGE,{"derivedFrom":sQuery(id+"F0.wireOp",EDGE,"E475")}),1.0]])]});
            extrude(context, id + "F2", {"entities" : qUnion([Q0, Q1, Q2, Q3, Q4, Q5, Q6, Q7, Q8, Q9, Q10, Q11, Q12]), "depth" : 15.24 * mm, "offsetDistance" : 25.4 * mm});
        }
    });
